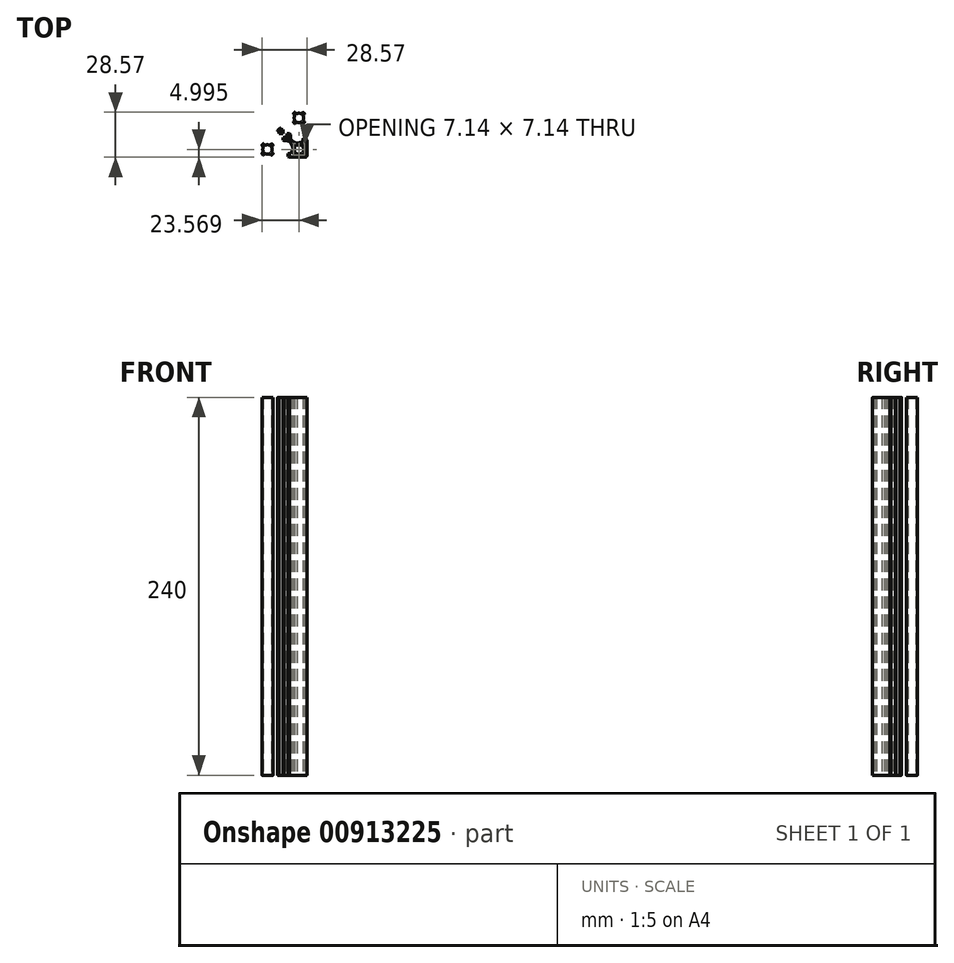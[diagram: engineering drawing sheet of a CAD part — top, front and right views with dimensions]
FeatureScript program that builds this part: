
annotation { "Feature Type Name" : "Feature", "Feature Type Description" : "" }
export const myFeature = defineFeature(function(context is Context, id is Id, definition is map)
    precondition{}
    {
        {
            var Q0;
            Q0=qCreatedBy(makeId("Top.planeOp"),FACE);
            var sketch = newSketch(context, id + "F0", { "sketchPlane" : qUnion([Q0])});
            skLineSegment(sketch, "E0", {"start": v(-71.63, -514.45) * mm, "end": v(-71.63, -402.69) * mm});
            skLineSegment(sketch, "E1", {"start": v(-127.51, -458.57) * mm, "end": v(-15.75, -458.57) * mm});
            skArc(sketch, "E2", {"start": v(-139.86, -492.5) * mm, "mid": v(-139.16, -497.13) * mm, "end": v(-141.3, -501.29) * mm});
            skLineSegment(sketch, "E3", {"start": v(-141.3, -501.29) * mm, "end": v(-160.1, -520.1) * mm});
            skArc(sketch, "E4", {"start": v(-160.1, -520.1) * mm, "mid": v(-162.32, -525.08) * mm, "end": v(-160.65, -530.26) * mm});
            skArc(sketch, "E5", {"start": v(-160.65, -530.26) * mm, "mid": v(-152.46, -539.39) * mm, "end": v(-143.33, -547.58) * mm});
            skArc(sketch, "E6", {"start": v(-143.33, -547.58) * mm, "mid": v(-138.14, -549.26) * mm, "end": v(-133.16, -547.04) * mm});
            skLineSegment(sketch, "E7", {"start": v(-133.16, -547.04) * mm, "end": v(-114.35, -528.23) * mm});
            skArc(sketch, "E8", {"start": v(-114.35, -528.23) * mm, "mid": v(-110.2, -526.1) * mm, "end": v(-105.57, -526.8) * mm});
            skArc(sketch, "E9", {"start": v(-105.57, -526.8) * mm, "mid": v(-71.63, -534.77) * mm, "end": v(-37.7, -526.8) * mm});
            skArc(sketch, "E10", {"start": v(-37.7, -526.8) * mm, "mid": v(-33.07, -526.1) * mm, "end": v(-28.91, -528.23) * mm});
            skLineSegment(sketch, "E11", {"start": v(-28.91, -528.23) * mm, "end": v(-10.1, -547.04) * mm});
            skArc(sketch, "E12", {"start": v(-10.1, -547.04) * mm, "mid": v(-5.12, -549.26) * mm, "end": v(0.06, -547.58) * mm});
            skArc(sketch, "E13", {"start": v(0.06, -547.58) * mm, "mid": v(9.19, -539.39) * mm, "end": v(17.38, -530.26) * mm});
            skArc(sketch, "E14", {"start": v(17.38, -530.26) * mm, "mid": v(19.06, -525.08) * mm, "end": v(16.84, -520.1) * mm});
            skLineSegment(sketch, "E15", {"start": v(16.84, -520.1) * mm, "end": v(-1.97, -501.29) * mm});
            skArc(sketch, "E16", {"start": v(-1.97, -501.29) * mm, "mid": v(-4.1, -497.13) * mm, "end": v(-3.4, -492.5) * mm});
            skArc(sketch, "E17", {"start": v(-3.4, -492.5) * mm, "mid": v(4.57, -458.57) * mm, "end": v(-3.4, -424.63) * mm});
            skArc(sketch, "E18", {"start": v(-3.4, -424.63) * mm, "mid": v(-4.1, -420) * mm, "end": v(-1.97, -415.85) * mm});
            skLineSegment(sketch, "E19", {"start": v(-1.97, -415.85) * mm, "end": v(16.84, -397.04) * mm});
            skArc(sketch, "E20", {"start": v(16.84, -397.04) * mm, "mid": v(19.06, -392.06) * mm, "end": v(17.38, -386.87) * mm});
            skArc(sketch, "E21", {"start": v(17.38, -386.87) * mm, "mid": v(9.19, -377.74) * mm, "end": v(0.06, -369.55) * mm});
            skArc(sketch, "E22", {"start": v(0.06, -369.55) * mm, "mid": v(-5.12, -367.88) * mm, "end": v(-10.1, -370.1) * mm});
            skLineSegment(sketch, "E23", {"start": v(-10.1, -370.1) * mm, "end": v(-28.91, -388.9) * mm});
            skArc(sketch, "E24", {"start": v(-28.91, -388.9) * mm, "mid": v(-33.07, -391.04) * mm, "end": v(-37.7, -390.34) * mm});
            skArc(sketch, "E25", {"start": v(-37.7, -390.34) * mm, "mid": v(-71.63, -382.37) * mm, "end": v(-105.57, -390.34) * mm});
            skArc(sketch, "E26", {"start": v(-105.57, -390.34) * mm, "mid": v(-110.2, -391.04) * mm, "end": v(-114.35, -388.9) * mm});
            skLineSegment(sketch, "E27", {"start": v(-114.35, -388.9) * mm, "end": v(-133.16, -370.1) * mm});
            skArc(sketch, "E28", {"start": v(-133.16, -370.1) * mm, "mid": v(-138.14, -367.88) * mm, "end": v(-143.33, -369.55) * mm});
            skArc(sketch, "E29", {"start": v(-143.33, -369.55) * mm, "mid": v(-152.46, -377.74) * mm, "end": v(-160.65, -386.87) * mm});
            skArc(sketch, "E30", {"start": v(-160.65, -386.87) * mm, "mid": v(-162.32, -392.06) * mm, "end": v(-160.1, -397.04) * mm});
            skLineSegment(sketch, "E31", {"start": v(-160.1, -397.04) * mm, "end": v(-141.3, -415.85) * mm});
            skArc(sketch, "E32", {"start": v(-141.3, -415.85) * mm, "mid": v(-139.16, -420) * mm, "end": v(-139.86, -424.63) * mm});
            skArc(sketch, "E33", {"start": v(-139.86, -424.63) * mm, "mid": v(-147.83, -458.57) * mm, "end": v(-139.86, -492.5) * mm});
            skLineSegment(sketch, "E34", {"start": v(-127.53, -966.58) * mm, "end": v(-15.77, -966.6) * mm});
            skLineSegment(sketch, "E35", {"start": v(-71.65, -910.7) * mm, "end": v(-71.66, -1022.47) * mm});
            skArc(sketch, "E36", {"start": v(-139.88, -932.64) * mm, "mid": v(-139.18, -928.02) * mm, "end": v(-141.3, -923.86) * mm});
            skLineSegment(sketch, "E37", {"start": v(-141.3, -923.86) * mm, "end": v(-160.12, -905.05) * mm});
            skArc(sketch, "E38", {"start": v(-160.12, -905.05) * mm, "mid": v(-162.34, -900.07) * mm, "end": v(-160.66, -894.88) * mm});
            skArc(sketch, "E39", {"start": v(-160.66, -894.88) * mm, "mid": v(-152.47, -885.76) * mm, "end": v(-143.34, -877.56) * mm});
            skArc(sketch, "E40", {"start": v(-143.34, -877.56) * mm, "mid": v(-138.16, -875.9) * mm, "end": v(-133.18, -878.11) * mm});
            skLineSegment(sketch, "E41", {"start": v(-133.18, -878.11) * mm, "end": v(-114.37, -896.92) * mm});
            skArc(sketch, "E42", {"start": v(-114.37, -896.92) * mm, "mid": v(-110.2, -899.06) * mm, "end": v(-105.59, -898.36) * mm});
            skArc(sketch, "E43", {"start": v(-105.59, -898.36) * mm, "mid": v(-71.65, -890.39) * mm, "end": v(-37.71, -898.36) * mm});
            skArc(sketch, "E44", {"start": v(-37.71, -898.36) * mm, "mid": v(-33.09, -899.06) * mm, "end": v(-28.93, -896.93) * mm});
            skLineSegment(sketch, "E45", {"start": v(-28.93, -896.93) * mm, "end": v(-10.12, -878.12) * mm});
            skArc(sketch, "E46", {"start": v(-10.12, -878.12) * mm, "mid": v(-5.14, -875.9) * mm, "end": v(0.05, -877.58) * mm});
            skArc(sketch, "E47", {"start": v(0.05, -877.58) * mm, "mid": v(9.18, -885.77) * mm, "end": v(17.37, -894.9) * mm});
            skArc(sketch, "E48", {"start": v(17.37, -894.9) * mm, "mid": v(19.04, -900.08) * mm, "end": v(16.82, -905.06) * mm});
            skLineSegment(sketch, "E49", {"start": v(16.82, -905.06) * mm, "end": v(-2, -923.87) * mm});
            skArc(sketch, "E50", {"start": v(-2, -923.87) * mm, "mid": v(-4.12, -928.03) * mm, "end": v(-3.43, -932.65) * mm});
            skArc(sketch, "E51", {"start": v(-3.43, -932.65) * mm, "mid": v(4.55, -966.6) * mm, "end": v(-3.43, -1000.53) * mm});
            skArc(sketch, "E52", {"start": v(-3.43, -1000.53) * mm, "mid": v(-4.13, -1005.15) * mm, "end": v(-2, -1009.31) * mm});
            skLineSegment(sketch, "E53", {"start": v(-2, -1009.31) * mm, "end": v(16.81, -1028.12) * mm});
            skArc(sketch, "E54", {"start": v(16.81, -1028.12) * mm, "mid": v(19.03, -1033.1) * mm, "end": v(17.36, -1038.3) * mm});
            skArc(sketch, "E55", {"start": v(17.36, -1038.3) * mm, "mid": v(9.16, -1047.42) * mm, "end": v(0.04, -1055.6) * mm});
            skArc(sketch, "E56", {"start": v(0.04, -1055.6) * mm, "mid": v(-5.15, -1057.28) * mm, "end": v(-10.13, -1055.06) * mm});
            skLineSegment(sketch, "E57", {"start": v(-10.13, -1055.06) * mm, "end": v(-28.94, -1036.25) * mm});
            skArc(sketch, "E58", {"start": v(-28.94, -1036.25) * mm, "mid": v(-33.1, -1034.12) * mm, "end": v(-37.72, -1034.81) * mm});
            skArc(sketch, "E59", {"start": v(-37.72, -1034.81) * mm, "mid": v(-71.66, -1042.79) * mm, "end": v(-105.6, -1034.8) * mm});
            skArc(sketch, "E60", {"start": v(-105.6, -1034.8) * mm, "mid": v(-110.22, -1034.11) * mm, "end": v(-114.38, -1036.24) * mm});
            skLineSegment(sketch, "E61", {"start": v(-114.38, -1036.24) * mm, "end": v(-133.19, -1055.05) * mm});
            skArc(sketch, "E62", {"start": v(-133.19, -1055.05) * mm, "mid": v(-138.17, -1057.27) * mm, "end": v(-143.36, -1055.6) * mm});
            skArc(sketch, "E63", {"start": v(-143.36, -1055.6) * mm, "mid": v(-152.48, -1047.4) * mm, "end": v(-160.68, -1038.28) * mm});
            skArc(sketch, "E64", {"start": v(-160.68, -1038.28) * mm, "mid": v(-162.35, -1033.09) * mm, "end": v(-160.13, -1028.1) * mm});
            skLineSegment(sketch, "E65", {"start": v(-160.13, -1028.1) * mm, "end": v(-141.32, -1009.3) * mm});
            skArc(sketch, "E66", {"start": v(-141.32, -1009.3) * mm, "mid": v(-139.18, -1005.14) * mm, "end": v(-139.88, -1000.52) * mm});
            skArc(sketch, "E67", {"start": v(-139.88, -1000.52) * mm, "mid": v(-147.85, -966.58) * mm, "end": v(-139.88, -932.64) * mm});
            skArc(sketch, "E68", {"start": v(-511.33, -932.64) * mm, "mid": v(-512.03, -928.02) * mm, "end": v(-509.9, -923.86) * mm});
            skLineSegment(sketch, "E69", {"start": v(-509.9, -923.86) * mm, "end": v(-491.09, -905.05) * mm});
            skArc(sketch, "E70", {"start": v(-491.09, -905.05) * mm, "mid": v(-488.87, -900.07) * mm, "end": v(-490.54, -894.88) * mm});
            skArc(sketch, "E71", {"start": v(-490.54, -894.88) * mm, "mid": v(-498.74, -885.76) * mm, "end": v(-507.86, -877.56) * mm});
            skArc(sketch, "E72", {"start": v(-507.86, -877.56) * mm, "mid": v(-513.05, -875.9) * mm, "end": v(-518.03, -878.11) * mm});
            skLineSegment(sketch, "E73", {"start": v(-518.03, -878.11) * mm, "end": v(-536.84, -896.92) * mm});
            skArc(sketch, "E74", {"start": v(-536.84, -896.92) * mm, "mid": v(-541, -899.06) * mm, "end": v(-545.62, -898.36) * mm});
            skArc(sketch, "E75", {"start": v(-545.62, -898.36) * mm, "mid": v(-579.56, -890.39) * mm, "end": v(-613.5, -898.36) * mm});
            skArc(sketch, "E76", {"start": v(-613.5, -898.36) * mm, "mid": v(-618.12, -899.06) * mm, "end": v(-622.28, -896.93) * mm});
            skLineSegment(sketch, "E77", {"start": v(-622.28, -896.93) * mm, "end": v(-641.1, -878.12) * mm});
            skArc(sketch, "E78", {"start": v(-641.1, -878.12) * mm, "mid": v(-646.07, -875.9) * mm, "end": v(-651.26, -877.58) * mm});
            skArc(sketch, "E79", {"start": v(-651.26, -877.58) * mm, "mid": v(-660.38, -885.77) * mm, "end": v(-668.58, -894.9) * mm});
            skArc(sketch, "E80", {"start": v(-668.58, -894.9) * mm, "mid": v(-670.25, -900.08) * mm, "end": v(-668.03, -905.06) * mm});
            skLineSegment(sketch, "E81", {"start": v(-668.03, -905.06) * mm, "end": v(-649.22, -923.87) * mm});
            skArc(sketch, "E82", {"start": v(-649.22, -923.87) * mm, "mid": v(-647.08, -928.03) * mm, "end": v(-647.78, -932.65) * mm});
            skArc(sketch, "E83", {"start": v(-647.78, -932.65) * mm, "mid": v(-655.75, -966.6) * mm, "end": v(-647.78, -1000.53) * mm});
            skArc(sketch, "E84", {"start": v(-647.78, -1000.53) * mm, "mid": v(-647.08, -1005.15) * mm, "end": v(-649.21, -1009.31) * mm});
            skLineSegment(sketch, "E85", {"start": v(-649.21, -1009.31) * mm, "end": v(-668.02, -1028.12) * mm});
            skArc(sketch, "E86", {"start": v(-668.02, -1028.12) * mm, "mid": v(-670.24, -1033.1) * mm, "end": v(-668.57, -1038.3) * mm});
            skArc(sketch, "E87", {"start": v(-668.57, -1038.3) * mm, "mid": v(-660.37, -1047.42) * mm, "end": v(-651.24, -1055.6) * mm});
            skArc(sketch, "E88", {"start": v(-651.24, -1055.6) * mm, "mid": v(-646.06, -1057.28) * mm, "end": v(-641.08, -1055.06) * mm});
            skLineSegment(sketch, "E89", {"start": v(-641.08, -1055.06) * mm, "end": v(-622.27, -1036.25) * mm});
            skArc(sketch, "E90", {"start": v(-622.27, -1036.25) * mm, "mid": v(-618.1, -1034.12) * mm, "end": v(-613.49, -1034.81) * mm});
            skArc(sketch, "E91", {"start": v(-613.49, -1034.81) * mm, "mid": v(-579.55, -1042.79) * mm, "end": v(-545.61, -1034.8) * mm});
            skArc(sketch, "E92", {"start": v(-545.61, -1034.8) * mm, "mid": v(-540.99, -1034.11) * mm, "end": v(-536.83, -1036.24) * mm});
            skLineSegment(sketch, "E93", {"start": v(-536.83, -1036.24) * mm, "end": v(-518.02, -1055.05) * mm});
            skArc(sketch, "E94", {"start": v(-518.02, -1055.05) * mm, "mid": v(-513.04, -1057.27) * mm, "end": v(-507.85, -1055.6) * mm});
            skArc(sketch, "E95", {"start": v(-507.85, -1055.6) * mm, "mid": v(-498.73, -1047.4) * mm, "end": v(-490.53, -1038.28) * mm});
            skArc(sketch, "E96", {"start": v(-490.53, -1038.28) * mm, "mid": v(-488.86, -1033.09) * mm, "end": v(-491.08, -1028.1) * mm});
            skLineSegment(sketch, "E97", {"start": v(-491.08, -1028.1) * mm, "end": v(-509.9, -1009.3) * mm});
            skArc(sketch, "E98", {"start": v(-509.9, -1009.3) * mm, "mid": v(-512.02, -1005.14) * mm, "end": v(-511.33, -1000.52) * mm});
            skArc(sketch, "E99", {"start": v(-511.33, -1000.52) * mm, "mid": v(-503.35, -966.58) * mm, "end": v(-511.33, -932.64) * mm});
            skLineSegment(sketch, "E100", {"start": v(-579.56, -910.7) * mm, "end": v(-579.55, -1022.47) * mm});
            skLineSegment(sketch, "E101", {"start": v(-523.67, -966.58) * mm, "end": v(-635.43, -966.6) * mm});
            skLineSegment(sketch, "E102", {"start": v(-523.7, -458.57) * mm, "end": v(-635.45, -458.57) * mm});
            skLineSegment(sketch, "E103", {"start": v(-579.57, -514.45) * mm, "end": v(-579.57, -402.69) * mm});
            skLineSegment(sketch, "E104", {"start": v(67.05, -712.57) * mm, "end": v(-737.67, -712.57) * mm});
            skLineSegment(sketch, "E105", {"start": v(-325.57, -1117.47) * mm, "end": v(-325.57, -306.26) * mm});
            skArc(sketch, "E106", {"start": v(-243.35, -672.28) * mm, "mid": v(-237.77, -667.95) * mm, "end": v(-238.14, -660.9) * mm});
            skArc(sketch, "E107", {"start": v(-238.14, -660.9) * mm, "mid": v(-253.76, -640.75) * mm, "end": v(-273.91, -625.13) * mm});
            skArc(sketch, "E108", {"start": v(-273.91, -625.13) * mm, "mid": v(-280.96, -624.76) * mm, "end": v(-285.29, -630.34) * mm});
            skLineSegment(sketch, "E109", {"start": v(-285.29, -630.34) * mm, "end": v(-288.68, -649.16) * mm});
            skArc(sketch, "E110", {"start": v(-288.68, -649.16) * mm, "mid": v(-292.64, -654.55) * mm, "end": v(-299.33, -654.74) * mm});
            skArc(sketch, "E111", {"start": v(-299.33, -654.74) * mm, "mid": v(-325.57, -649.07) * mm, "end": v(-351.82, -654.74) * mm});
            skArc(sketch, "E112", {"start": v(-351.82, -654.74) * mm, "mid": v(-358.51, -654.55) * mm, "end": v(-362.47, -649.16) * mm});
            skLineSegment(sketch, "E113", {"start": v(-362.47, -649.16) * mm, "end": v(-365.86, -630.34) * mm});
            skArc(sketch, "E114", {"start": v(-365.86, -630.34) * mm, "mid": v(-370.19, -624.76) * mm, "end": v(-377.24, -625.13) * mm});
            skArc(sketch, "E115", {"start": v(-377.24, -625.13) * mm, "mid": v(-397.39, -640.75) * mm, "end": v(-413.01, -660.9) * mm});
            skArc(sketch, "E116", {"start": v(-413.01, -660.9) * mm, "mid": v(-413.38, -667.95) * mm, "end": v(-407.8, -672.28) * mm});
            skLineSegment(sketch, "E117", {"start": v(-407.8, -672.28) * mm, "end": v(-388.98, -675.67) * mm});
            skArc(sketch, "E118", {"start": v(-388.98, -675.67) * mm, "mid": v(-383.59, -679.63) * mm, "end": v(-383.4, -686.32) * mm});
            skArc(sketch, "E119", {"start": v(-383.4, -686.32) * mm, "mid": v(-389.07, -712.57) * mm, "end": v(-383.4, -738.81) * mm});
            skArc(sketch, "E120", {"start": v(-383.4, -738.81) * mm, "mid": v(-383.59, -745.5) * mm, "end": v(-388.98, -749.46) * mm});
            skLineSegment(sketch, "E121", {"start": v(-388.98, -749.46) * mm, "end": v(-407.8, -752.85) * mm});
            skArc(sketch, "E122", {"start": v(-407.8, -752.85) * mm, "mid": v(-413.38, -757.18) * mm, "end": v(-413.01, -764.23) * mm});
            skArc(sketch, "E123", {"start": v(-413.01, -764.23) * mm, "mid": v(-397.39, -784.38) * mm, "end": v(-377.24, -800) * mm});
            skArc(sketch, "E124", {"start": v(-377.24, -800) * mm, "mid": v(-370.19, -800.37) * mm, "end": v(-365.86, -794.8) * mm});
            skLineSegment(sketch, "E125", {"start": v(-365.86, -794.8) * mm, "end": v(-362.47, -775.98) * mm});
            skArc(sketch, "E126", {"start": v(-362.47, -775.98) * mm, "mid": v(-358.51, -770.58) * mm, "end": v(-351.82, -770.39) * mm});
            skArc(sketch, "E127", {"start": v(-351.82, -770.39) * mm, "mid": v(-325.57, -776.07) * mm, "end": v(-299.33, -770.39) * mm});
            skArc(sketch, "E128", {"start": v(-299.33, -770.39) * mm, "mid": v(-292.64, -770.58) * mm, "end": v(-288.68, -775.98) * mm});
            skLineSegment(sketch, "E129", {"start": v(-288.68, -775.98) * mm, "end": v(-285.29, -794.8) * mm});
            skArc(sketch, "E130", {"start": v(-285.29, -794.8) * mm, "mid": v(-280.96, -800.37) * mm, "end": v(-273.91, -800) * mm});
            skArc(sketch, "E131", {"start": v(-273.91, -800) * mm, "mid": v(-253.76, -784.38) * mm, "end": v(-238.14, -764.23) * mm});
            skArc(sketch, "E132", {"start": v(-238.14, -764.23) * mm, "mid": v(-237.77, -757.18) * mm, "end": v(-243.35, -752.85) * mm});
            skLineSegment(sketch, "E133", {"start": v(-243.35, -752.85) * mm, "end": v(-262.17, -749.46) * mm});
            skArc(sketch, "E134", {"start": v(-262.17, -749.46) * mm, "mid": v(-267.56, -745.5) * mm, "end": v(-267.75, -738.81) * mm});
            skArc(sketch, "E135", {"start": v(-267.75, -738.81) * mm, "mid": v(-262.07, -712.57) * mm, "end": v(-267.75, -686.32) * mm});
            skArc(sketch, "E136", {"start": v(-267.75, -686.32) * mm, "mid": v(-267.56, -679.63) * mm, "end": v(-262.17, -675.67) * mm});
            skLineSegment(sketch, "E137", {"start": v(-262.17, -675.67) * mm, "end": v(-243.35, -672.28) * mm});
            skArc(sketch, "E138", {"start": v(-511.35, -492.5) * mm, "mid": v(-512.05, -497.13) * mm, "end": v(-509.91, -501.29) * mm});
            skLineSegment(sketch, "E139", {"start": v(-509.91, -501.29) * mm, "end": v(-491.1, -520.1) * mm});
            skArc(sketch, "E140", {"start": v(-491.1, -520.1) * mm, "mid": v(-488.88, -525.08) * mm, "end": v(-490.56, -530.26) * mm});
            skArc(sketch, "E141", {"start": v(-490.56, -530.26) * mm, "mid": v(-498.75, -539.39) * mm, "end": v(-507.88, -547.58) * mm});
            skArc(sketch, "E142", {"start": v(-507.88, -547.58) * mm, "mid": v(-513.07, -549.26) * mm, "end": v(-518.04, -547.04) * mm});
            skLineSegment(sketch, "E143", {"start": v(-518.04, -547.04) * mm, "end": v(-536.86, -528.23) * mm});
            skArc(sketch, "E144", {"start": v(-536.86, -528.23) * mm, "mid": v(-541.01, -526.1) * mm, "end": v(-545.64, -526.8) * mm});
            skArc(sketch, "E145", {"start": v(-545.64, -526.8) * mm, "mid": v(-579.57, -534.77) * mm, "end": v(-613.51, -526.8) * mm});
            skArc(sketch, "E146", {"start": v(-613.51, -526.8) * mm, "mid": v(-618.13, -526.1) * mm, "end": v(-622.3, -528.23) * mm});
            skLineSegment(sketch, "E147", {"start": v(-622.3, -528.23) * mm, "end": v(-641.1, -547.04) * mm});
            skArc(sketch, "E148", {"start": v(-641.1, -547.04) * mm, "mid": v(-646.08, -549.26) * mm, "end": v(-651.27, -547.58) * mm});
            skArc(sketch, "E149", {"start": v(-651.27, -547.58) * mm, "mid": v(-660.4, -539.39) * mm, "end": v(-668.6, -530.26) * mm});
            skArc(sketch, "E150", {"start": v(-668.6, -530.26) * mm, "mid": v(-670.27, -525.08) * mm, "end": v(-668.04, -520.1) * mm});
            skLineSegment(sketch, "E151", {"start": v(-668.04, -520.1) * mm, "end": v(-649.23, -501.29) * mm});
            skArc(sketch, "E152", {"start": v(-649.23, -501.29) * mm, "mid": v(-647.1, -497.13) * mm, "end": v(-647.8, -492.5) * mm});
            skArc(sketch, "E153", {"start": v(-647.8, -492.5) * mm, "mid": v(-655.77, -458.57) * mm, "end": v(-647.8, -424.63) * mm});
            skArc(sketch, "E154", {"start": v(-647.8, -424.63) * mm, "mid": v(-647.1, -420) * mm, "end": v(-649.23, -415.85) * mm});
            skLineSegment(sketch, "E155", {"start": v(-649.23, -415.85) * mm, "end": v(-668.04, -397.04) * mm});
            skArc(sketch, "E156", {"start": v(-668.04, -397.04) * mm, "mid": v(-670.27, -392.06) * mm, "end": v(-668.6, -386.87) * mm});
            skArc(sketch, "E157", {"start": v(-668.6, -386.87) * mm, "mid": v(-660.4, -377.74) * mm, "end": v(-651.27, -369.55) * mm});
            skArc(sketch, "E158", {"start": v(-651.27, -369.55) * mm, "mid": v(-646.08, -367.88) * mm, "end": v(-641.1, -370.1) * mm});
            skLineSegment(sketch, "E159", {"start": v(-641.1, -370.1) * mm, "end": v(-622.3, -388.9) * mm});
            skArc(sketch, "E160", {"start": v(-622.3, -388.9) * mm, "mid": v(-618.13, -391.04) * mm, "end": v(-613.51, -390.34) * mm});
            skArc(sketch, "E161", {"start": v(-613.51, -390.34) * mm, "mid": v(-579.57, -382.37) * mm, "end": v(-545.64, -390.34) * mm});
            skArc(sketch, "E162", {"start": v(-545.64, -390.34) * mm, "mid": v(-541.01, -391.04) * mm, "end": v(-536.86, -388.9) * mm});
            skLineSegment(sketch, "E163", {"start": v(-536.86, -388.9) * mm, "end": v(-518.04, -370.1) * mm});
            skArc(sketch, "E164", {"start": v(-518.04, -370.1) * mm, "mid": v(-513.07, -367.88) * mm, "end": v(-507.88, -369.55) * mm});
            skArc(sketch, "E165", {"start": v(-507.88, -369.55) * mm, "mid": v(-498.75, -377.74) * mm, "end": v(-490.56, -386.87) * mm});
            skArc(sketch, "E166", {"start": v(-490.56, -386.87) * mm, "mid": v(-488.88, -392.06) * mm, "end": v(-491.1, -397.04) * mm});
            skLineSegment(sketch, "E167", {"start": v(-491.1, -397.04) * mm, "end": v(-509.91, -415.85) * mm});
            skArc(sketch, "E168", {"start": v(-509.91, -415.85) * mm, "mid": v(-512.05, -420) * mm, "end": v(-511.35, -424.63) * mm});
            skArc(sketch, "E169", {"start": v(-511.35, -424.63) * mm, "mid": v(-503.37, -458.57) * mm, "end": v(-511.35, -492.5) * mm});
            skLineSegment(sketch, "E170", {"start": v(-225.24, -1093.57) * mm, "end": v(-245.56, -1080.87) * mm});
            skLineSegment(sketch, "E171", {"start": v(-245.56, -1080.87) * mm, "end": v(-245.56, -1037.69) * mm});
            skArc(sketch, "E172", {"start": v(-245.56, -1037.69) * mm, "mid": v(-243.33, -1032.3) * mm, "end": v(-237.94, -1030.07) * mm});
            skLineSegment(sketch, "E173", {"start": v(-237.94, -1030.07) * mm, "end": v(-196.03, -1030.07) * mm});
            skLineSegment(sketch, "E174", {"start": v(-196.03, -1030.07) * mm, "end": v(-170.95, -952.55) * mm});
            skArc(sketch, "E175", {"start": v(-170.95, -952.55) * mm, "mid": v(-169.75, -945.99) * mm, "end": v(-170.3, -939.33) * mm});
            skArc(sketch, "E176", {"start": v(-170.3, -939.33) * mm, "mid": v(-191.6, -887.57) * mm, "end": v(-223.87, -841.84) * mm});
            skArc(sketch, "E177", {"start": v(-223.87, -841.84) * mm, "mid": v(-245.35, -830.7) * mm, "end": v(-269.24, -826.87) * mm});
            skLineSegment(sketch, "E178", {"start": v(-269.24, -826.87) * mm, "end": v(-312.87, -826.87) * mm});
            skLineSegment(sketch, "E179", {"start": v(-312.87, -826.87) * mm, "end": v(-325.57, -814.17) * mm});
            skLineSegment(sketch, "E180", {"start": v(-325.57, -814.17) * mm, "end": v(-338.27, -826.87) * mm});
            skLineSegment(sketch, "E181", {"start": v(-338.27, -826.87) * mm, "end": v(-381.9, -826.87) * mm});
            skArc(sketch, "E182", {"start": v(-381.9, -826.87) * mm, "mid": v(-405.8, -830.7) * mm, "end": v(-427.28, -841.84) * mm});
            skArc(sketch, "E183", {"start": v(-427.28, -841.84) * mm, "mid": v(-459.55, -887.57) * mm, "end": v(-480.85, -939.33) * mm});
            skArc(sketch, "E184", {"start": v(-480.85, -939.33) * mm, "mid": v(-481.4, -945.99) * mm, "end": v(-480.2, -952.55) * mm});
            skLineSegment(sketch, "E185", {"start": v(-480.2, -952.55) * mm, "end": v(-455.11, -1030.07) * mm});
            skLineSegment(sketch, "E186", {"start": v(-455.11, -1030.07) * mm, "end": v(-413.2, -1030.07) * mm});
            skArc(sketch, "E187", {"start": v(-413.2, -1030.07) * mm, "mid": v(-407.82, -1032.3) * mm, "end": v(-405.58, -1037.69) * mm});
            skLineSegment(sketch, "E188", {"start": v(-405.58, -1037.69) * mm, "end": v(-405.58, -1080.87) * mm});
            skLineSegment(sketch, "E189", {"start": v(-405.58, -1080.87) * mm, "end": v(-425.9, -1093.57) * mm});
            skLineSegment(sketch, "E190", {"start": v(-425.9, -1093.57) * mm, "end": v(-681.17, -1093.57) * mm});
            skArc(sketch, "E191", {"start": v(-681.17, -1093.57) * mm, "mid": v(-699.13, -1086.13) * mm, "end": v(-706.57, -1068.17) * mm});
            skLineSegment(sketch, "E192", {"start": v(-706.57, -1068.17) * mm, "end": v(-706.57, -812.9) * mm});
            skLineSegment(sketch, "E193", {"start": v(-706.57, -812.9) * mm, "end": v(-693.87, -792.58) * mm});
            skLineSegment(sketch, "E194", {"start": v(-693.87, -792.58) * mm, "end": v(-650.7, -792.58) * mm});
            skArc(sketch, "E195", {"start": v(-650.7, -792.58) * mm, "mid": v(-645.3, -794.8) * mm, "end": v(-643.07, -800.2) * mm});
            skLineSegment(sketch, "E196", {"start": v(-643.07, -800.2) * mm, "end": v(-643.07, -842.1) * mm});
            skLineSegment(sketch, "E197", {"start": v(-643.07, -842.1) * mm, "end": v(-565.56, -867.2) * mm});
            skArc(sketch, "E198", {"start": v(-565.56, -867.2) * mm, "mid": v(-559, -868.4) * mm, "end": v(-552.34, -867.85) * mm});
            skArc(sketch, "E199", {"start": v(-552.34, -867.85) * mm, "mid": v(-500.58, -846.54) * mm, "end": v(-454.85, -814.27) * mm});
            skArc(sketch, "E200", {"start": v(-454.85, -814.27) * mm, "mid": v(-443.72, -792.79) * mm, "end": v(-439.87, -768.9) * mm});
            skLineSegment(sketch, "E201", {"start": v(-439.87, -768.9) * mm, "end": v(-439.87, -725.27) * mm});
            skLineSegment(sketch, "E202", {"start": v(-439.87, -725.27) * mm, "end": v(-427.17, -712.57) * mm});
            skLineSegment(sketch, "E203", {"start": v(-427.17, -712.57) * mm, "end": v(-439.87, -699.87) * mm});
            skLineSegment(sketch, "E204", {"start": v(-439.87, -699.87) * mm, "end": v(-439.87, -656.23) * mm});
            skArc(sketch, "E205", {"start": v(-439.87, -656.23) * mm, "mid": v(-443.72, -632.34) * mm, "end": v(-454.85, -610.86) * mm});
            skArc(sketch, "E206", {"start": v(-454.85, -610.86) * mm, "mid": v(-500.58, -578.6) * mm, "end": v(-552.34, -557.29) * mm});
            skArc(sketch, "E207", {"start": v(-552.34, -557.29) * mm, "mid": v(-559, -556.74) * mm, "end": v(-565.56, -557.94) * mm});
            skLineSegment(sketch, "E208", {"start": v(-565.56, -557.94) * mm, "end": v(-643.07, -583.03) * mm});
            skLineSegment(sketch, "E209", {"start": v(-643.07, -583.03) * mm, "end": v(-643.07, -624.94) * mm});
            skArc(sketch, "E210", {"start": v(-643.07, -624.94) * mm, "mid": v(-645.3, -630.32) * mm, "end": v(-650.7, -632.56) * mm});
            skLineSegment(sketch, "E211", {"start": v(-650.7, -632.56) * mm, "end": v(-693.87, -632.56) * mm});
            skLineSegment(sketch, "E212", {"start": v(-693.87, -632.56) * mm, "end": v(-706.57, -612.24) * mm});
            skLineSegment(sketch, "E213", {"start": v(-706.57, -612.24) * mm, "end": v(-706.57, -356.97) * mm});
            skArc(sketch, "E214", {"start": v(-706.57, -356.97) * mm, "mid": v(-699.13, -339) * mm, "end": v(-681.17, -331.57) * mm});
            skLineSegment(sketch, "E215", {"start": v(-681.17, -331.57) * mm, "end": v(-425.9, -331.57) * mm});
            skLineSegment(sketch, "E216", {"start": v(-425.9, -331.57) * mm, "end": v(-405.58, -344.27) * mm});
            skLineSegment(sketch, "E217", {"start": v(-405.58, -344.27) * mm, "end": v(-405.58, -387.45) * mm});
            skArc(sketch, "E218", {"start": v(-405.58, -387.45) * mm, "mid": v(-407.82, -392.83) * mm, "end": v(-413.2, -395.07) * mm});
            skLineSegment(sketch, "E219", {"start": v(-413.2, -395.07) * mm, "end": v(-455.11, -395.07) * mm});
            skLineSegment(sketch, "E220", {"start": v(-455.11, -395.07) * mm, "end": v(-480.2, -472.58) * mm});
            skArc(sketch, "E221", {"start": v(-480.2, -472.58) * mm, "mid": v(-481.4, -479.15) * mm, "end": v(-480.85, -485.8) * mm});
            skArc(sketch, "E222", {"start": v(-480.85, -485.8) * mm, "mid": v(-459.55, -537.56) * mm, "end": v(-427.28, -583.29) * mm});
            skArc(sketch, "E223", {"start": v(-427.28, -583.29) * mm, "mid": v(-405.8, -594.43) * mm, "end": v(-381.9, -598.27) * mm});
            skLineSegment(sketch, "E224", {"start": v(-381.9, -598.27) * mm, "end": v(-338.27, -598.27) * mm});
            skLineSegment(sketch, "E225", {"start": v(-338.27, -598.27) * mm, "end": v(-325.57, -610.97) * mm});
            skLineSegment(sketch, "E226", {"start": v(-325.57, -610.97) * mm, "end": v(-312.87, -598.27) * mm});
            skLineSegment(sketch, "E227", {"start": v(-312.87, -598.27) * mm, "end": v(-269.24, -598.27) * mm});
            skArc(sketch, "E228", {"start": v(-269.24, -598.27) * mm, "mid": v(-245.35, -594.43) * mm, "end": v(-223.87, -583.29) * mm});
            skArc(sketch, "E229", {"start": v(-223.87, -583.29) * mm, "mid": v(-191.6, -537.56) * mm, "end": v(-170.3, -485.8) * mm});
            skArc(sketch, "E230", {"start": v(-170.3, -485.8) * mm, "mid": v(-169.75, -479.15) * mm, "end": v(-170.95, -472.58) * mm});
            skLineSegment(sketch, "E231", {"start": v(-170.95, -472.58) * mm, "end": v(-196.03, -395.07) * mm});
            skLineSegment(sketch, "E232", {"start": v(-196.03, -395.07) * mm, "end": v(-237.94, -395.07) * mm});
            skArc(sketch, "E233", {"start": v(-237.94, -395.07) * mm, "mid": v(-243.33, -392.83) * mm, "end": v(-245.56, -387.45) * mm});
            skLineSegment(sketch, "E234", {"start": v(-245.56, -387.45) * mm, "end": v(-245.56, -344.27) * mm});
            skLineSegment(sketch, "E235", {"start": v(-245.56, -344.27) * mm, "end": v(-225.24, -331.57) * mm});
            skLineSegment(sketch, "E236", {"start": v(-225.24, -331.57) * mm, "end": v(30.03, -331.57) * mm});
            skArc(sketch, "E237", {"start": v(30.03, -331.57) * mm, "mid": v(47.99, -339) * mm, "end": v(55.43, -356.97) * mm});
            skLineSegment(sketch, "E238", {"start": v(55.43, -356.97) * mm, "end": v(55.43, -612.24) * mm});
            skLineSegment(sketch, "E239", {"start": v(55.43, -612.24) * mm, "end": v(42.73, -632.56) * mm});
            skLineSegment(sketch, "E240", {"start": v(42.73, -632.56) * mm, "end": v(-0.45, -632.56) * mm});
            skArc(sketch, "E241", {"start": v(-0.45, -632.56) * mm, "mid": v(-5.84, -630.32) * mm, "end": v(-8.07, -624.94) * mm});
            skLineSegment(sketch, "E242", {"start": v(-8.07, -624.94) * mm, "end": v(-8.07, -583.03) * mm});
            skLineSegment(sketch, "E243", {"start": v(-8.07, -583.03) * mm, "end": v(-85.59, -557.94) * mm});
            skArc(sketch, "E244", {"start": v(-85.59, -557.94) * mm, "mid": v(-92.15, -556.74) * mm, "end": v(-98.8, -557.29) * mm});
            skArc(sketch, "E245", {"start": v(-98.8, -557.29) * mm, "mid": v(-150.57, -578.6) * mm, "end": v(-196.3, -610.86) * mm});
            skArc(sketch, "E246", {"start": v(-196.3, -610.86) * mm, "mid": v(-207.43, -632.34) * mm, "end": v(-211.27, -656.23) * mm});
            skLineSegment(sketch, "E247", {"start": v(-211.27, -656.23) * mm, "end": v(-211.27, -699.87) * mm});
            skLineSegment(sketch, "E248", {"start": v(-211.27, -699.87) * mm, "end": v(-223.97, -712.57) * mm});
            skLineSegment(sketch, "E249", {"start": v(-223.97, -712.57) * mm, "end": v(-211.27, -725.27) * mm});
            skLineSegment(sketch, "E250", {"start": v(-211.27, -725.27) * mm, "end": v(-211.27, -768.9) * mm});
            skArc(sketch, "E251", {"start": v(-211.27, -768.9) * mm, "mid": v(-207.43, -792.79) * mm, "end": v(-196.3, -814.27) * mm});
            skArc(sketch, "E252", {"start": v(-196.3, -814.27) * mm, "mid": v(-150.57, -846.54) * mm, "end": v(-98.8, -867.85) * mm});
            skArc(sketch, "E253", {"start": v(-98.8, -867.85) * mm, "mid": v(-92.15, -868.4) * mm, "end": v(-85.59, -867.2) * mm});
            skLineSegment(sketch, "E254", {"start": v(-85.59, -867.2) * mm, "end": v(-8.07, -842.1) * mm});
            skLineSegment(sketch, "E255", {"start": v(-8.07, -842.1) * mm, "end": v(-8.07, -800.2) * mm});
            skArc(sketch, "E256", {"start": v(-8.07, -800.2) * mm, "mid": v(-5.84, -794.8) * mm, "end": v(-0.45, -792.58) * mm});
            skLineSegment(sketch, "E257", {"start": v(-0.45, -792.58) * mm, "end": v(42.73, -792.58) * mm});
            skLineSegment(sketch, "E258", {"start": v(42.73, -792.58) * mm, "end": v(55.43, -812.9) * mm});
            skLineSegment(sketch, "E259", {"start": v(55.43, -812.9) * mm, "end": v(55.43, -1068.17) * mm});
            skArc(sketch, "E260", {"start": v(55.43, -1068.17) * mm, "mid": v(47.99, -1086.13) * mm, "end": v(30.03, -1093.57) * mm});
            skLineSegment(sketch, "E261", {"start": v(30.03, -1093.57) * mm, "end": v(-225.24, -1093.57) * mm});
            skLineSegment(sketch, "E262", {"start": v(465.62, 205.58) * mm, "end": v(465.62, 209.98) * mm});
            skLineSegment(sketch, "E263", {"start": v(463.42, 207.78) * mm, "end": v(467.82, 207.78) * mm});
            skArc(sketch, "E264", {"start": v(462.94, 206.45) * mm, "mid": v(462.96, 206.27) * mm, "end": v(462.88, 206.1) * mm});
            skLineSegment(sketch, "E265", {"start": v(462.88, 206.1) * mm, "end": v(462.14, 205.36) * mm});
            skArc(sketch, "E266", {"start": v(462.14, 205.36) * mm, "mid": v(462.05, 205.17) * mm, "end": v(462.12, 204.96) * mm});
            skArc(sketch, "E267", {"start": v(462.12, 204.96) * mm, "mid": v(462.44, 204.6) * mm, "end": v(462.8, 204.28) * mm});
            skArc(sketch, "E268", {"start": v(462.8, 204.28) * mm, "mid": v(463, 204.21) * mm, "end": v(463.2, 204.3) * mm});
            skLineSegment(sketch, "E269", {"start": v(463.2, 204.3) * mm, "end": v(463.94, 205.04) * mm});
            skArc(sketch, "E270", {"start": v(463.94, 205.04) * mm, "mid": v(464.1, 205.13) * mm, "end": v(464.29, 205.1) * mm});
            skArc(sketch, "E271", {"start": v(464.29, 205.1) * mm, "mid": v(465.62, 204.78) * mm, "end": v(466.96, 205.1) * mm});
            skArc(sketch, "E272", {"start": v(466.96, 205.1) * mm, "mid": v(467.14, 205.13) * mm, "end": v(467.3, 205.04) * mm});
            skLineSegment(sketch, "E273", {"start": v(467.3, 205.04) * mm, "end": v(468.04, 204.3) * mm});
            skArc(sketch, "E274", {"start": v(468.04, 204.3) * mm, "mid": v(468.24, 204.21) * mm, "end": v(468.44, 204.28) * mm});
            skArc(sketch, "E275", {"start": v(468.44, 204.28) * mm, "mid": v(468.8, 204.6) * mm, "end": v(469.13, 204.96) * mm});
            skArc(sketch, "E276", {"start": v(469.13, 204.96) * mm, "mid": v(469.2, 205.17) * mm, "end": v(469.1, 205.36) * mm});
            skLineSegment(sketch, "E277", {"start": v(469.1, 205.36) * mm, "end": v(468.36, 206.1) * mm});
            skArc(sketch, "E278", {"start": v(468.36, 206.1) * mm, "mid": v(468.28, 206.27) * mm, "end": v(468.3, 206.45) * mm});
            skArc(sketch, "E279", {"start": v(468.3, 206.45) * mm, "mid": v(468.62, 207.78) * mm, "end": v(468.3, 209.12) * mm});
            skArc(sketch, "E280", {"start": v(468.3, 209.12) * mm, "mid": v(468.28, 209.3) * mm, "end": v(468.36, 209.47) * mm});
            skLineSegment(sketch, "E281", {"start": v(468.36, 209.47) * mm, "end": v(469.1, 210.2) * mm});
            skArc(sketch, "E282", {"start": v(469.1, 210.2) * mm, "mid": v(469.2, 210.4) * mm, "end": v(469.13, 210.6) * mm});
            skArc(sketch, "E283", {"start": v(469.13, 210.6) * mm, "mid": v(468.8, 210.97) * mm, "end": v(468.44, 211.29) * mm});
            skArc(sketch, "E284", {"start": v(468.44, 211.29) * mm, "mid": v(468.24, 211.35) * mm, "end": v(468.04, 211.27) * mm});
            skLineSegment(sketch, "E285", {"start": v(468.04, 211.27) * mm, "end": v(467.3, 210.53) * mm});
            skArc(sketch, "E286", {"start": v(467.3, 210.53) * mm, "mid": v(467.14, 210.44) * mm, "end": v(466.96, 210.47) * mm});
            skArc(sketch, "E287", {"start": v(466.96, 210.47) * mm, "mid": v(465.62, 210.78) * mm, "end": v(464.29, 210.47) * mm});
            skArc(sketch, "E288", {"start": v(464.29, 210.47) * mm, "mid": v(464.1, 210.44) * mm, "end": v(463.94, 210.53) * mm});
            skLineSegment(sketch, "E289", {"start": v(463.94, 210.53) * mm, "end": v(463.2, 211.27) * mm});
            skArc(sketch, "E290", {"start": v(463.2, 211.27) * mm, "mid": v(463, 211.35) * mm, "end": v(462.8, 211.29) * mm});
            skArc(sketch, "E291", {"start": v(462.8, 211.29) * mm, "mid": v(462.44, 210.97) * mm, "end": v(462.12, 210.6) * mm});
            skArc(sketch, "E292", {"start": v(462.12, 210.6) * mm, "mid": v(462.05, 210.4) * mm, "end": v(462.14, 210.2) * mm});
            skLineSegment(sketch, "E293", {"start": v(462.14, 210.2) * mm, "end": v(462.88, 209.47) * mm});
            skArc(sketch, "E294", {"start": v(462.88, 209.47) * mm, "mid": v(462.96, 209.3) * mm, "end": v(462.94, 209.12) * mm});
            skArc(sketch, "E295", {"start": v(462.94, 209.12) * mm, "mid": v(462.62, 207.78) * mm, "end": v(462.94, 206.45) * mm});
            skLineSegment(sketch, "E296", {"start": v(463.42, 187.78) * mm, "end": v(467.82, 187.78) * mm});
            skLineSegment(sketch, "E297", {"start": v(465.62, 189.98) * mm, "end": v(465.62, 185.58) * mm});
            skArc(sketch, "E298", {"start": v(462.94, 189.12) * mm, "mid": v(462.96, 189.3) * mm, "end": v(462.88, 189.47) * mm});
            skLineSegment(sketch, "E299", {"start": v(462.88, 189.47) * mm, "end": v(462.14, 190.2) * mm});
            skArc(sketch, "E300", {"start": v(462.14, 190.2) * mm, "mid": v(462.05, 190.4) * mm, "end": v(462.12, 190.6) * mm});
            skArc(sketch, "E301", {"start": v(462.12, 190.6) * mm, "mid": v(462.44, 190.97) * mm, "end": v(462.8, 191.29) * mm});
            skArc(sketch, "E302", {"start": v(462.8, 191.29) * mm, "mid": v(463, 191.35) * mm, "end": v(463.2, 191.27) * mm});
            skLineSegment(sketch, "E303", {"start": v(463.2, 191.27) * mm, "end": v(463.94, 190.53) * mm});
            skArc(sketch, "E304", {"start": v(463.94, 190.53) * mm, "mid": v(464.1, 190.44) * mm, "end": v(464.29, 190.47) * mm});
            skArc(sketch, "E305", {"start": v(464.29, 190.47) * mm, "mid": v(465.62, 190.78) * mm, "end": v(466.96, 190.47) * mm});
            skArc(sketch, "E306", {"start": v(466.96, 190.47) * mm, "mid": v(467.14, 190.44) * mm, "end": v(467.3, 190.53) * mm});
            skLineSegment(sketch, "E307", {"start": v(467.3, 190.53) * mm, "end": v(468.04, 191.27) * mm});
            skArc(sketch, "E308", {"start": v(468.04, 191.27) * mm, "mid": v(468.24, 191.35) * mm, "end": v(468.44, 191.29) * mm});
            skArc(sketch, "E309", {"start": v(468.44, 191.29) * mm, "mid": v(468.8, 190.96) * mm, "end": v(469.13, 190.6) * mm});
            skArc(sketch, "E310", {"start": v(469.13, 190.6) * mm, "mid": v(469.2, 190.4) * mm, "end": v(469.1, 190.2) * mm});
            skLineSegment(sketch, "E311", {"start": v(469.1, 190.2) * mm, "end": v(468.36, 189.46) * mm});
            skArc(sketch, "E312", {"start": v(468.36, 189.46) * mm, "mid": v(468.28, 189.3) * mm, "end": v(468.3, 189.12) * mm});
            skArc(sketch, "E313", {"start": v(468.3, 189.12) * mm, "mid": v(468.62, 187.78) * mm, "end": v(468.3, 186.45) * mm});
            skArc(sketch, "E314", {"start": v(468.3, 186.45) * mm, "mid": v(468.28, 186.26) * mm, "end": v(468.36, 186.1) * mm});
            skLineSegment(sketch, "E315", {"start": v(468.36, 186.1) * mm, "end": v(469.1, 185.36) * mm});
            skArc(sketch, "E316", {"start": v(469.1, 185.36) * mm, "mid": v(469.2, 185.16) * mm, "end": v(469.13, 184.96) * mm});
            skArc(sketch, "E317", {"start": v(469.13, 184.96) * mm, "mid": v(468.8, 184.6) * mm, "end": v(468.44, 184.28) * mm});
            skArc(sketch, "E318", {"start": v(468.44, 184.28) * mm, "mid": v(468.24, 184.21) * mm, "end": v(468.04, 184.3) * mm});
            skLineSegment(sketch, "E319", {"start": v(468.04, 184.3) * mm, "end": v(467.3, 185.04) * mm});
            skArc(sketch, "E320", {"start": v(467.3, 185.04) * mm, "mid": v(467.14, 185.12) * mm, "end": v(466.96, 185.1) * mm});
            skArc(sketch, "E321", {"start": v(466.96, 185.1) * mm, "mid": v(465.62, 184.78) * mm, "end": v(464.28, 185.1) * mm});
            skArc(sketch, "E322", {"start": v(464.28, 185.1) * mm, "mid": v(464.1, 185.12) * mm, "end": v(463.94, 185.04) * mm});
            skLineSegment(sketch, "E323", {"start": v(463.94, 185.04) * mm, "end": v(463.2, 184.3) * mm});
            skArc(sketch, "E324", {"start": v(463.2, 184.3) * mm, "mid": v(463, 184.21) * mm, "end": v(462.8, 184.28) * mm});
            skArc(sketch, "E325", {"start": v(462.8, 184.28) * mm, "mid": v(462.44, 184.6) * mm, "end": v(462.12, 184.96) * mm});
            skArc(sketch, "E326", {"start": v(462.12, 184.96) * mm, "mid": v(462.05, 185.16) * mm, "end": v(462.14, 185.36) * mm});
            skLineSegment(sketch, "E327", {"start": v(462.14, 185.36) * mm, "end": v(462.88, 186.1) * mm});
            skArc(sketch, "E328", {"start": v(462.88, 186.1) * mm, "mid": v(462.96, 186.27) * mm, "end": v(462.93, 186.45) * mm});
            skArc(sketch, "E329", {"start": v(462.93, 186.45) * mm, "mid": v(462.62, 187.78) * mm, "end": v(462.94, 189.12) * mm});
            skArc(sketch, "E330", {"start": v(448.31, 189.12) * mm, "mid": v(448.28, 189.3) * mm, "end": v(448.37, 189.47) * mm});
            skLineSegment(sketch, "E331", {"start": v(448.37, 189.47) * mm, "end": v(449.1, 190.2) * mm});
            skArc(sketch, "E332", {"start": v(449.1, 190.2) * mm, "mid": v(449.2, 190.4) * mm, "end": v(449.13, 190.6) * mm});
            skArc(sketch, "E333", {"start": v(449.13, 190.6) * mm, "mid": v(448.8, 190.97) * mm, "end": v(448.45, 191.29) * mm});
            skArc(sketch, "E334", {"start": v(448.45, 191.29) * mm, "mid": v(448.24, 191.35) * mm, "end": v(448.05, 191.27) * mm});
            skLineSegment(sketch, "E335", {"start": v(448.05, 191.27) * mm, "end": v(447.3, 190.53) * mm});
            skArc(sketch, "E336", {"start": v(447.3, 190.53) * mm, "mid": v(447.14, 190.44) * mm, "end": v(446.96, 190.47) * mm});
            skArc(sketch, "E337", {"start": v(446.96, 190.47) * mm, "mid": v(445.62, 190.78) * mm, "end": v(444.29, 190.47) * mm});
            skArc(sketch, "E338", {"start": v(444.29, 190.47) * mm, "mid": v(444.1, 190.44) * mm, "end": v(443.94, 190.53) * mm});
            skLineSegment(sketch, "E339", {"start": v(443.94, 190.53) * mm, "end": v(443.2, 191.27) * mm});
            skArc(sketch, "E340", {"start": v(443.2, 191.27) * mm, "mid": v(443, 191.35) * mm, "end": v(442.8, 191.29) * mm});
            skArc(sketch, "E341", {"start": v(442.8, 191.29) * mm, "mid": v(442.44, 190.96) * mm, "end": v(442.12, 190.6) * mm});
            skArc(sketch, "E342", {"start": v(442.12, 190.6) * mm, "mid": v(442.05, 190.4) * mm, "end": v(442.14, 190.2) * mm});
            skLineSegment(sketch, "E343", {"start": v(442.14, 190.2) * mm, "end": v(442.88, 189.46) * mm});
            skArc(sketch, "E344", {"start": v(442.88, 189.46) * mm, "mid": v(442.97, 189.3) * mm, "end": v(442.94, 189.12) * mm});
            skArc(sketch, "E345", {"start": v(442.94, 189.12) * mm, "mid": v(442.62, 187.78) * mm, "end": v(442.94, 186.45) * mm});
            skArc(sketch, "E346", {"start": v(442.94, 186.45) * mm, "mid": v(442.97, 186.26) * mm, "end": v(442.88, 186.1) * mm});
            skLineSegment(sketch, "E347", {"start": v(442.88, 186.1) * mm, "end": v(442.14, 185.36) * mm});
            skArc(sketch, "E348", {"start": v(442.14, 185.36) * mm, "mid": v(442.05, 185.16) * mm, "end": v(442.12, 184.96) * mm});
            skArc(sketch, "E349", {"start": v(442.12, 184.96) * mm, "mid": v(442.44, 184.6) * mm, "end": v(442.8, 184.28) * mm});
            skArc(sketch, "E350", {"start": v(442.8, 184.28) * mm, "mid": v(443, 184.21) * mm, "end": v(443.2, 184.3) * mm});
            skLineSegment(sketch, "E351", {"start": v(443.2, 184.3) * mm, "end": v(443.94, 185.04) * mm});
            skArc(sketch, "E352", {"start": v(443.94, 185.04) * mm, "mid": v(444.1, 185.12) * mm, "end": v(444.29, 185.1) * mm});
            skArc(sketch, "E353", {"start": v(444.29, 185.1) * mm, "mid": v(445.63, 184.78) * mm, "end": v(446.96, 185.1) * mm});
            skArc(sketch, "E354", {"start": v(446.96, 185.1) * mm, "mid": v(447.14, 185.12) * mm, "end": v(447.3, 185.04) * mm});
            skLineSegment(sketch, "E355", {"start": v(447.3, 185.04) * mm, "end": v(448.05, 184.3) * mm});
            skArc(sketch, "E356", {"start": v(448.05, 184.3) * mm, "mid": v(448.24, 184.21) * mm, "end": v(448.45, 184.28) * mm});
            skArc(sketch, "E357", {"start": v(448.45, 184.28) * mm, "mid": v(448.8, 184.6) * mm, "end": v(449.13, 184.96) * mm});
            skArc(sketch, "E358", {"start": v(449.13, 184.96) * mm, "mid": v(449.2, 185.16) * mm, "end": v(449.1, 185.36) * mm});
            skLineSegment(sketch, "E359", {"start": v(449.1, 185.36) * mm, "end": v(448.37, 186.1) * mm});
            skArc(sketch, "E360", {"start": v(448.37, 186.1) * mm, "mid": v(448.28, 186.27) * mm, "end": v(448.31, 186.45) * mm});
            skArc(sketch, "E361", {"start": v(448.31, 186.45) * mm, "mid": v(448.62, 187.78) * mm, "end": v(448.31, 189.12) * mm});
            skLineSegment(sketch, "E362", {"start": v(445.62, 189.98) * mm, "end": v(445.63, 185.58) * mm});
            skLineSegment(sketch, "E363", {"start": v(447.82, 187.78) * mm, "end": v(443.42, 187.78) * mm});
            skLineSegment(sketch, "E364", {"start": v(447.82, 207.78) * mm, "end": v(443.42, 207.78) * mm});
            skLineSegment(sketch, "E365", {"start": v(445.62, 205.58) * mm, "end": v(445.62, 209.98) * mm});
            skLineSegment(sketch, "E366", {"start": v(471.08, 197.78) * mm, "end": v(439.4, 197.78) * mm});
            skLineSegment(sketch, "E367", {"start": v(455.62, 181.84) * mm, "end": v(455.62, 213.78) * mm});
            skArc(sketch, "E368", {"start": v(458.86, 199.37) * mm, "mid": v(459.08, 199.54) * mm, "end": v(459.07, 199.82) * mm});
            skArc(sketch, "E369", {"start": v(459.07, 199.82) * mm, "mid": v(458.45, 200.61) * mm, "end": v(457.66, 201.23) * mm});
            skArc(sketch, "E370", {"start": v(457.66, 201.23) * mm, "mid": v(457.38, 201.24) * mm, "end": v(457.21, 201.02) * mm});
            skLineSegment(sketch, "E371", {"start": v(457.21, 201.02) * mm, "end": v(457.08, 200.28) * mm});
            skArc(sketch, "E372", {"start": v(457.08, 200.28) * mm, "mid": v(456.92, 200.07) * mm, "end": v(456.66, 200.06) * mm});
            skArc(sketch, "E373", {"start": v(456.66, 200.06) * mm, "mid": v(455.62, 200.28) * mm, "end": v(454.6, 200.06) * mm});
            skArc(sketch, "E374", {"start": v(454.6, 200.06) * mm, "mid": v(454.33, 200.07) * mm, "end": v(454.17, 200.28) * mm});
            skLineSegment(sketch, "E375", {"start": v(454.17, 200.28) * mm, "end": v(454.04, 201.02) * mm});
            skArc(sketch, "E376", {"start": v(454.04, 201.02) * mm, "mid": v(453.87, 201.24) * mm, "end": v(453.6, 201.23) * mm});
            skArc(sketch, "E377", {"start": v(453.6, 201.23) * mm, "mid": v(452.8, 200.61) * mm, "end": v(452.18, 199.82) * mm});
            skArc(sketch, "E378", {"start": v(452.18, 199.82) * mm, "mid": v(452.17, 199.54) * mm, "end": v(452.39, 199.37) * mm});
            skLineSegment(sketch, "E379", {"start": v(452.39, 199.37) * mm, "end": v(453.13, 199.24) * mm});
            skArc(sketch, "E380", {"start": v(453.13, 199.24) * mm, "mid": v(453.34, 199.08) * mm, "end": v(453.35, 198.82) * mm});
            skArc(sketch, "E381", {"start": v(453.35, 198.82) * mm, "mid": v(453.12, 197.78) * mm, "end": v(453.35, 196.75) * mm});
            skArc(sketch, "E382", {"start": v(453.35, 196.75) * mm, "mid": v(453.34, 196.49) * mm, "end": v(453.13, 196.33) * mm});
            skLineSegment(sketch, "E383", {"start": v(453.13, 196.33) * mm, "end": v(452.39, 196.2) * mm});
            skArc(sketch, "E384", {"start": v(452.39, 196.2) * mm, "mid": v(452.17, 196.03) * mm, "end": v(452.18, 195.75) * mm});
            skArc(sketch, "E385", {"start": v(452.18, 195.75) * mm, "mid": v(452.8, 194.96) * mm, "end": v(453.6, 194.34) * mm});
            skArc(sketch, "E386", {"start": v(453.6, 194.34) * mm, "mid": v(453.87, 194.33) * mm, "end": v(454.04, 194.55) * mm});
            skLineSegment(sketch, "E387", {"start": v(454.04, 194.55) * mm, "end": v(454.17, 195.29) * mm});
            skArc(sketch, "E388", {"start": v(454.17, 195.29) * mm, "mid": v(454.33, 195.5) * mm, "end": v(454.6, 195.5) * mm});
            skArc(sketch, "E389", {"start": v(454.6, 195.5) * mm, "mid": v(455.62, 195.28) * mm, "end": v(456.66, 195.5) * mm});
            skArc(sketch, "E390", {"start": v(456.66, 195.5) * mm, "mid": v(456.92, 195.5) * mm, "end": v(457.08, 195.29) * mm});
            skLineSegment(sketch, "E391", {"start": v(457.08, 195.29) * mm, "end": v(457.21, 194.55) * mm});
            skArc(sketch, "E392", {"start": v(457.21, 194.55) * mm, "mid": v(457.38, 194.33) * mm, "end": v(457.66, 194.34) * mm});
            skArc(sketch, "E393", {"start": v(457.66, 194.34) * mm, "mid": v(458.45, 194.96) * mm, "end": v(459.07, 195.75) * mm});
            skArc(sketch, "E394", {"start": v(459.07, 195.75) * mm, "mid": v(459.08, 196.03) * mm, "end": v(458.86, 196.2) * mm});
            skLineSegment(sketch, "E395", {"start": v(458.86, 196.2) * mm, "end": v(458.12, 196.33) * mm});
            skArc(sketch, "E396", {"start": v(458.12, 196.33) * mm, "mid": v(457.9, 196.49) * mm, "end": v(457.9, 196.75) * mm});
            skArc(sketch, "E397", {"start": v(457.9, 196.75) * mm, "mid": v(458.12, 197.78) * mm, "end": v(457.9, 198.82) * mm});
            skArc(sketch, "E398", {"start": v(457.9, 198.82) * mm, "mid": v(457.9, 199.08) * mm, "end": v(458.12, 199.24) * mm});
            skLineSegment(sketch, "E399", {"start": v(458.12, 199.24) * mm, "end": v(458.86, 199.37) * mm});
            skArc(sketch, "E400", {"start": v(448.31, 206.45) * mm, "mid": v(448.28, 206.27) * mm, "end": v(448.37, 206.1) * mm});
            skLineSegment(sketch, "E401", {"start": v(448.37, 206.1) * mm, "end": v(449.1, 205.36) * mm});
            skArc(sketch, "E402", {"start": v(449.1, 205.36) * mm, "mid": v(449.2, 205.17) * mm, "end": v(449.13, 204.96) * mm});
            skArc(sketch, "E403", {"start": v(449.13, 204.96) * mm, "mid": v(448.8, 204.6) * mm, "end": v(448.45, 204.28) * mm});
            skArc(sketch, "E404", {"start": v(448.45, 204.28) * mm, "mid": v(448.24, 204.21) * mm, "end": v(448.05, 204.3) * mm});
            skLineSegment(sketch, "E405", {"start": v(448.05, 204.3) * mm, "end": v(447.3, 205.04) * mm});
            skArc(sketch, "E406", {"start": v(447.3, 205.04) * mm, "mid": v(447.14, 205.13) * mm, "end": v(446.96, 205.1) * mm});
            skArc(sketch, "E407", {"start": v(446.96, 205.1) * mm, "mid": v(445.62, 204.78) * mm, "end": v(444.29, 205.1) * mm});
            skArc(sketch, "E408", {"start": v(444.29, 205.1) * mm, "mid": v(444.1, 205.13) * mm, "end": v(443.94, 205.04) * mm});
            skLineSegment(sketch, "E409", {"start": v(443.94, 205.04) * mm, "end": v(443.2, 204.3) * mm});
            skArc(sketch, "E410", {"start": v(443.2, 204.3) * mm, "mid": v(443, 204.21) * mm, "end": v(442.8, 204.28) * mm});
            skArc(sketch, "E411", {"start": v(442.8, 204.28) * mm, "mid": v(442.44, 204.6) * mm, "end": v(442.12, 204.96) * mm});
            skArc(sketch, "E412", {"start": v(442.12, 204.96) * mm, "mid": v(442.05, 205.17) * mm, "end": v(442.14, 205.36) * mm});
            skLineSegment(sketch, "E413", {"start": v(442.14, 205.36) * mm, "end": v(442.88, 206.1) * mm});
            skArc(sketch, "E414", {"start": v(442.88, 206.1) * mm, "mid": v(442.97, 206.27) * mm, "end": v(442.94, 206.45) * mm});
            skArc(sketch, "E415", {"start": v(442.94, 206.45) * mm, "mid": v(442.62, 207.78) * mm, "end": v(442.94, 209.12) * mm});
            skArc(sketch, "E416", {"start": v(442.94, 209.12) * mm, "mid": v(442.97, 209.3) * mm, "end": v(442.88, 209.47) * mm});
            skLineSegment(sketch, "E417", {"start": v(442.88, 209.47) * mm, "end": v(442.14, 210.2) * mm});
            skArc(sketch, "E418", {"start": v(442.14, 210.2) * mm, "mid": v(442.05, 210.4) * mm, "end": v(442.12, 210.6) * mm});
            skArc(sketch, "E419", {"start": v(442.12, 210.6) * mm, "mid": v(442.44, 210.97) * mm, "end": v(442.8, 211.29) * mm});
            skArc(sketch, "E420", {"start": v(442.8, 211.29) * mm, "mid": v(443, 211.35) * mm, "end": v(443.2, 211.27) * mm});
            skLineSegment(sketch, "E421", {"start": v(443.2, 211.27) * mm, "end": v(443.94, 210.53) * mm});
            skArc(sketch, "E422", {"start": v(443.94, 210.53) * mm, "mid": v(444.1, 210.44) * mm, "end": v(444.29, 210.47) * mm});
            skArc(sketch, "E423", {"start": v(444.29, 210.47) * mm, "mid": v(445.62, 210.78) * mm, "end": v(446.96, 210.47) * mm});
            skArc(sketch, "E424", {"start": v(446.96, 210.47) * mm, "mid": v(447.14, 210.44) * mm, "end": v(447.3, 210.53) * mm});
            skLineSegment(sketch, "E425", {"start": v(447.3, 210.53) * mm, "end": v(448.05, 211.27) * mm});
            skArc(sketch, "E426", {"start": v(448.05, 211.27) * mm, "mid": v(448.24, 211.35) * mm, "end": v(448.45, 211.29) * mm});
            skArc(sketch, "E427", {"start": v(448.45, 211.29) * mm, "mid": v(448.8, 210.97) * mm, "end": v(449.13, 210.6) * mm});
            skArc(sketch, "E428", {"start": v(449.13, 210.6) * mm, "mid": v(449.2, 210.4) * mm, "end": v(449.1, 210.2) * mm});
            skLineSegment(sketch, "E429", {"start": v(449.1, 210.2) * mm, "end": v(448.37, 209.47) * mm});
            skArc(sketch, "E430", {"start": v(448.37, 209.47) * mm, "mid": v(448.28, 209.3) * mm, "end": v(448.31, 209.12) * mm});
            skArc(sketch, "E431", {"start": v(448.31, 209.12) * mm, "mid": v(448.62, 207.78) * mm, "end": v(448.31, 206.45) * mm});
            skLineSegment(sketch, "E432", {"start": v(459.57, 182.78) * mm, "end": v(458.77, 183.28) * mm});
            skLineSegment(sketch, "E433", {"start": v(458.77, 183.28) * mm, "end": v(458.77, 184.98) * mm});
            skArc(sketch, "E434", {"start": v(458.77, 184.98) * mm, "mid": v(458.86, 185.2) * mm, "end": v(459.07, 185.28) * mm});
            skLineSegment(sketch, "E435", {"start": v(459.07, 185.28) * mm, "end": v(460.72, 185.28) * mm});
            skLineSegment(sketch, "E436", {"start": v(460.72, 185.28) * mm, "end": v(461.71, 188.34) * mm});
            skArc(sketch, "E437", {"start": v(461.71, 188.34) * mm, "mid": v(461.76, 188.6) * mm, "end": v(461.74, 188.86) * mm});
            skArc(sketch, "E438", {"start": v(461.74, 188.86) * mm, "mid": v(460.9, 190.9) * mm, "end": v(459.63, 192.7) * mm});
            skArc(sketch, "E439", {"start": v(459.63, 192.7) * mm, "mid": v(458.78, 193.13) * mm, "end": v(457.84, 193.28) * mm});
            skLineSegment(sketch, "E440", {"start": v(457.84, 193.28) * mm, "end": v(456.12, 193.28) * mm});
            skLineSegment(sketch, "E441", {"start": v(456.12, 193.28) * mm, "end": v(455.62, 193.78) * mm});
            skLineSegment(sketch, "E442", {"start": v(455.62, 193.78) * mm, "end": v(455.12, 193.28) * mm});
            skLineSegment(sketch, "E443", {"start": v(455.12, 193.28) * mm, "end": v(453.4, 193.28) * mm});
            skArc(sketch, "E444", {"start": v(453.4, 193.28) * mm, "mid": v(452.47, 193.13) * mm, "end": v(451.62, 192.7) * mm});
            skArc(sketch, "E445", {"start": v(451.62, 192.7) * mm, "mid": v(450.35, 190.9) * mm, "end": v(449.51, 188.86) * mm});
            skArc(sketch, "E446", {"start": v(449.51, 188.86) * mm, "mid": v(449.49, 188.6) * mm, "end": v(449.54, 188.34) * mm});
            skLineSegment(sketch, "E447", {"start": v(449.54, 188.34) * mm, "end": v(450.52, 185.28) * mm});
            skLineSegment(sketch, "E448", {"start": v(450.52, 185.28) * mm, "end": v(452.17, 185.28) * mm});
            skArc(sketch, "E449", {"start": v(452.17, 185.28) * mm, "mid": v(452.39, 185.2) * mm, "end": v(452.47, 184.98) * mm});
            skLineSegment(sketch, "E450", {"start": v(452.47, 184.98) * mm, "end": v(452.47, 183.28) * mm});
            skLineSegment(sketch, "E451", {"start": v(452.47, 183.28) * mm, "end": v(451.67, 182.78) * mm});
            skLineSegment(sketch, "E452", {"start": v(451.67, 182.78) * mm, "end": v(441.62, 182.78) * mm});
            skArc(sketch, "E453", {"start": v(441.62, 182.78) * mm, "mid": v(440.92, 183.08) * mm, "end": v(440.62, 183.78) * mm});
            skLineSegment(sketch, "E454", {"start": v(440.62, 183.78) * mm, "end": v(440.62, 193.83) * mm});
            skLineSegment(sketch, "E455", {"start": v(440.62, 193.83) * mm, "end": v(441.12, 194.63) * mm});
            skLineSegment(sketch, "E456", {"start": v(441.12, 194.63) * mm, "end": v(442.82, 194.63) * mm});
            skArc(sketch, "E457", {"start": v(442.82, 194.63) * mm, "mid": v(443.04, 194.55) * mm, "end": v(443.12, 194.33) * mm});
            skLineSegment(sketch, "E458", {"start": v(443.12, 194.33) * mm, "end": v(443.12, 192.68) * mm});
            skLineSegment(sketch, "E459", {"start": v(443.12, 192.68) * mm, "end": v(446.18, 191.7) * mm});
            skArc(sketch, "E460", {"start": v(446.18, 191.7) * mm, "mid": v(446.43, 191.65) * mm, "end": v(446.7, 191.67) * mm});
            skArc(sketch, "E461", {"start": v(446.7, 191.67) * mm, "mid": v(448.73, 192.5) * mm, "end": v(450.53, 193.78) * mm});
            skArc(sketch, "E462", {"start": v(450.53, 193.78) * mm, "mid": v(450.97, 194.63) * mm, "end": v(451.12, 195.57) * mm});
            skLineSegment(sketch, "E463", {"start": v(451.12, 195.57) * mm, "end": v(451.12, 197.28) * mm});
            skLineSegment(sketch, "E464", {"start": v(451.12, 197.28) * mm, "end": v(451.62, 197.78) * mm});
            skLineSegment(sketch, "E465", {"start": v(451.62, 197.78) * mm, "end": v(451.12, 198.28) * mm});
            skLineSegment(sketch, "E466", {"start": v(451.12, 198.28) * mm, "end": v(451.12, 200) * mm});
            skArc(sketch, "E467", {"start": v(451.12, 200) * mm, "mid": v(450.97, 200.94) * mm, "end": v(450.53, 201.79) * mm});
            skArc(sketch, "E468", {"start": v(450.53, 201.79) * mm, "mid": v(448.73, 203.06) * mm, "end": v(446.7, 203.9) * mm});
            skArc(sketch, "E469", {"start": v(446.7, 203.9) * mm, "mid": v(446.43, 203.92) * mm, "end": v(446.18, 203.87) * mm});
            skLineSegment(sketch, "E470", {"start": v(446.18, 203.87) * mm, "end": v(443.12, 202.88) * mm});
            skLineSegment(sketch, "E471", {"start": v(443.12, 202.88) * mm, "end": v(443.12, 201.23) * mm});
            skArc(sketch, "E472", {"start": v(443.12, 201.23) * mm, "mid": v(443.04, 201.02) * mm, "end": v(442.82, 200.93) * mm});
            skLineSegment(sketch, "E473", {"start": v(442.82, 200.93) * mm, "end": v(441.12, 200.93) * mm});
            skLineSegment(sketch, "E474", {"start": v(441.12, 200.93) * mm, "end": v(440.62, 201.73) * mm});
            skLineSegment(sketch, "E475", {"start": v(440.62, 201.73) * mm, "end": v(440.62, 211.78) * mm});
            skArc(sketch, "E476", {"start": v(440.62, 211.78) * mm, "mid": v(440.92, 212.5) * mm, "end": v(441.62, 212.78) * mm});
            skLineSegment(sketch, "E477", {"start": v(441.62, 212.78) * mm, "end": v(451.67, 212.78) * mm});
            skLineSegment(sketch, "E478", {"start": v(451.67, 212.78) * mm, "end": v(452.47, 212.28) * mm});
            skLineSegment(sketch, "E479", {"start": v(452.47, 212.28) * mm, "end": v(452.47, 210.58) * mm});
            skArc(sketch, "E480", {"start": v(452.47, 210.58) * mm, "mid": v(452.39, 210.37) * mm, "end": v(452.17, 210.28) * mm});
            skLineSegment(sketch, "E481", {"start": v(452.17, 210.28) * mm, "end": v(450.52, 210.28) * mm});
            skLineSegment(sketch, "E482", {"start": v(450.52, 210.28) * mm, "end": v(449.54, 207.23) * mm});
            skArc(sketch, "E483", {"start": v(449.54, 207.23) * mm, "mid": v(449.49, 206.97) * mm, "end": v(449.51, 206.71) * mm});
            skArc(sketch, "E484", {"start": v(449.51, 206.71) * mm, "mid": v(450.35, 204.67) * mm, "end": v(451.62, 202.87) * mm});
            skArc(sketch, "E485", {"start": v(451.62, 202.87) * mm, "mid": v(452.47, 202.44) * mm, "end": v(453.4, 202.28) * mm});
            skLineSegment(sketch, "E486", {"start": v(453.4, 202.28) * mm, "end": v(455.12, 202.28) * mm});
            skLineSegment(sketch, "E487", {"start": v(455.12, 202.28) * mm, "end": v(455.62, 201.78) * mm});
            skLineSegment(sketch, "E488", {"start": v(455.62, 201.78) * mm, "end": v(456.12, 202.28) * mm});
            skLineSegment(sketch, "E489", {"start": v(456.12, 202.28) * mm, "end": v(457.84, 202.28) * mm});
            skArc(sketch, "E490", {"start": v(457.84, 202.28) * mm, "mid": v(458.78, 202.44) * mm, "end": v(459.63, 202.87) * mm});
            skArc(sketch, "E491", {"start": v(459.63, 202.87) * mm, "mid": v(460.9, 204.67) * mm, "end": v(461.74, 206.71) * mm});
            skArc(sketch, "E492", {"start": v(461.74, 206.71) * mm, "mid": v(461.76, 206.97) * mm, "end": v(461.71, 207.23) * mm});
            skLineSegment(sketch, "E493", {"start": v(461.71, 207.23) * mm, "end": v(460.72, 210.28) * mm});
            skLineSegment(sketch, "E494", {"start": v(460.72, 210.28) * mm, "end": v(459.07, 210.28) * mm});
            skArc(sketch, "E495", {"start": v(459.07, 210.28) * mm, "mid": v(458.86, 210.37) * mm, "end": v(458.77, 210.58) * mm});
            skLineSegment(sketch, "E496", {"start": v(458.77, 210.58) * mm, "end": v(458.77, 212.28) * mm});
            skLineSegment(sketch, "E497", {"start": v(458.77, 212.28) * mm, "end": v(459.57, 212.78) * mm});
            skLineSegment(sketch, "E498", {"start": v(459.57, 212.78) * mm, "end": v(469.62, 212.78) * mm});
            skArc(sketch, "E499", {"start": v(469.62, 212.78) * mm, "mid": v(470.33, 212.5) * mm, "end": v(470.62, 211.78) * mm});
            skLineSegment(sketch, "E500", {"start": v(470.62, 211.78) * mm, "end": v(470.62, 201.73) * mm});
            skLineSegment(sketch, "E501", {"start": v(470.62, 201.73) * mm, "end": v(470.12, 200.93) * mm});
            skLineSegment(sketch, "E502", {"start": v(470.12, 200.93) * mm, "end": v(468.42, 200.93) * mm});
            skArc(sketch, "E503", {"start": v(468.42, 200.93) * mm, "mid": v(468.21, 201.02) * mm, "end": v(468.12, 201.23) * mm});
            skLineSegment(sketch, "E504", {"start": v(468.12, 201.23) * mm, "end": v(468.12, 202.88) * mm});
            skLineSegment(sketch, "E505", {"start": v(468.12, 202.88) * mm, "end": v(465.07, 203.87) * mm});
            skArc(sketch, "E506", {"start": v(465.07, 203.87) * mm, "mid": v(464.81, 203.92) * mm, "end": v(464.55, 203.9) * mm});
            skArc(sketch, "E507", {"start": v(464.55, 203.9) * mm, "mid": v(462.51, 203.06) * mm, "end": v(460.71, 201.79) * mm});
            skArc(sketch, "E508", {"start": v(460.71, 201.79) * mm, "mid": v(460.28, 200.94) * mm, "end": v(460.12, 200) * mm});
            skLineSegment(sketch, "E509", {"start": v(460.12, 200) * mm, "end": v(460.12, 198.28) * mm});
            skLineSegment(sketch, "E510", {"start": v(460.12, 198.28) * mm, "end": v(459.62, 197.78) * mm});
            skLineSegment(sketch, "E511", {"start": v(459.62, 197.78) * mm, "end": v(460.12, 197.28) * mm});
            skLineSegment(sketch, "E512", {"start": v(460.12, 197.28) * mm, "end": v(460.12, 195.57) * mm});
            skArc(sketch, "E513", {"start": v(460.12, 195.57) * mm, "mid": v(460.28, 194.63) * mm, "end": v(460.71, 193.78) * mm});
            skArc(sketch, "E514", {"start": v(460.71, 193.78) * mm, "mid": v(462.51, 192.5) * mm, "end": v(464.55, 191.67) * mm});
            skArc(sketch, "E515", {"start": v(464.55, 191.67) * mm, "mid": v(464.81, 191.65) * mm, "end": v(465.07, 191.7) * mm});
            skLineSegment(sketch, "E516", {"start": v(465.07, 191.7) * mm, "end": v(468.12, 192.68) * mm});
            skLineSegment(sketch, "E517", {"start": v(468.12, 192.68) * mm, "end": v(468.12, 194.33) * mm});
            skArc(sketch, "E518", {"start": v(468.12, 194.33) * mm, "mid": v(468.21, 194.55) * mm, "end": v(468.42, 194.63) * mm});
            skLineSegment(sketch, "E519", {"start": v(468.42, 194.63) * mm, "end": v(470.12, 194.63) * mm});
            skLineSegment(sketch, "E520", {"start": v(470.12, 194.63) * mm, "end": v(470.62, 193.83) * mm});
            skLineSegment(sketch, "E521", {"start": v(470.62, 193.83) * mm, "end": v(470.62, 183.78) * mm});
            skArc(sketch, "E522", {"start": v(470.62, 183.78) * mm, "mid": v(470.33, 183.08) * mm, "end": v(469.62, 182.78) * mm});
            skLineSegment(sketch, "E523", {"start": v(469.62, 182.78) * mm, "end": v(459.57, 182.78) * mm});
            skLineSegment(sketch, "E524", {"start": v(-2.82, -20.25) * mm, "end": v(-2.82, -15.85) * mm});
            skLineSegment(sketch, "E525", {"start": v(-5.02, -18.05) * mm, "end": v(-0.62, -18.05) * mm});
            skArc(sketch, "E526", {"start": v(-5.5, -19.39) * mm, "mid": v(-5.48, -19.57) * mm, "end": v(-5.56, -19.74) * mm});
            skLineSegment(sketch, "E527", {"start": v(-5.56, -19.74) * mm, "end": v(-6.3, -20.48) * mm});
            skArc(sketch, "E528", {"start": v(-6.3, -20.48) * mm, "mid": v(-6.4, -20.67) * mm, "end": v(-6.32, -20.88) * mm});
            skArc(sketch, "E529", {"start": v(-6.32, -20.88) * mm, "mid": v(-6, -21.24) * mm, "end": v(-5.64, -21.56) * mm});
            skArc(sketch, "E530", {"start": v(-5.64, -21.56) * mm, "mid": v(-5.44, -21.62) * mm, "end": v(-5.24, -21.54) * mm});
            skLineSegment(sketch, "E531", {"start": v(-5.24, -21.54) * mm, "end": v(-4.5, -20.8) * mm});
            skArc(sketch, "E532", {"start": v(-4.5, -20.8) * mm, "mid": v(-4.34, -20.71) * mm, "end": v(-4.16, -20.74) * mm});
            skArc(sketch, "E533", {"start": v(-4.16, -20.74) * mm, "mid": v(-2.82, -21.05) * mm, "end": v(-1.48, -20.74) * mm});
            skArc(sketch, "E534", {"start": v(-1.48, -20.74) * mm, "mid": v(-1.3, -20.71) * mm, "end": v(-1.14, -20.8) * mm});
            skLineSegment(sketch, "E535", {"start": v(-1.14, -20.8) * mm, "end": v(-0.4, -21.54) * mm});
            skArc(sketch, "E536", {"start": v(-0.4, -21.54) * mm, "mid": v(-0.2, -21.62) * mm, "end": v(0, -21.56) * mm});
            skArc(sketch, "E537", {"start": v(0, -21.56) * mm, "mid": v(0.36, -21.24) * mm, "end": v(0.68, -20.88) * mm});
            skArc(sketch, "E538", {"start": v(0.68, -20.88) * mm, "mid": v(0.75, -20.67) * mm, "end": v(0.66, -20.48) * mm});
            skLineSegment(sketch, "E539", {"start": v(0.66, -20.48) * mm, "end": v(-0.08, -19.74) * mm});
            skArc(sketch, "E540", {"start": v(-0.08, -19.74) * mm, "mid": v(-0.16, -19.57) * mm, "end": v(-0.13, -19.39) * mm});
            skArc(sketch, "E541", {"start": v(-0.13, -19.39) * mm, "mid": v(0.18, -18.05) * mm, "end": v(-0.13, -16.72) * mm});
            skArc(sketch, "E542", {"start": v(-0.13, -16.72) * mm, "mid": v(-0.16, -16.54) * mm, "end": v(-0.08, -16.37) * mm});
            skLineSegment(sketch, "E543", {"start": v(-0.08, -16.37) * mm, "end": v(0.66, -15.63) * mm});
            skArc(sketch, "E544", {"start": v(0.66, -15.63) * mm, "mid": v(0.75, -15.44) * mm, "end": v(0.68, -15.23) * mm});
            skArc(sketch, "E545", {"start": v(0.68, -15.23) * mm, "mid": v(0.36, -14.87) * mm, "end": v(0, -14.55) * mm});
            skArc(sketch, "E546", {"start": v(0, -14.55) * mm, "mid": v(-0.2, -14.48) * mm, "end": v(-0.4, -14.57) * mm});
            skLineSegment(sketch, "E547", {"start": v(-0.4, -14.57) * mm, "end": v(-1.14, -15.31) * mm});
            skArc(sketch, "E548", {"start": v(-1.14, -15.31) * mm, "mid": v(-1.3, -15.4) * mm, "end": v(-1.48, -15.37) * mm});
            skArc(sketch, "E549", {"start": v(-1.48, -15.37) * mm, "mid": v(-2.82, -15.05) * mm, "end": v(-4.16, -15.37) * mm});
            skArc(sketch, "E550", {"start": v(-4.16, -15.37) * mm, "mid": v(-4.34, -15.4) * mm, "end": v(-4.5, -15.31) * mm});
            skLineSegment(sketch, "E551", {"start": v(-4.5, -15.31) * mm, "end": v(-5.24, -14.57) * mm});
            skArc(sketch, "E552", {"start": v(-5.24, -14.57) * mm, "mid": v(-5.44, -14.48) * mm, "end": v(-5.64, -14.55) * mm});
            skArc(sketch, "E553", {"start": v(-5.64, -14.55) * mm, "mid": v(-6, -14.87) * mm, "end": v(-6.32, -15.23) * mm});
            skArc(sketch, "E554", {"start": v(-6.32, -15.23) * mm, "mid": v(-6.4, -15.44) * mm, "end": v(-6.3, -15.63) * mm});
            skLineSegment(sketch, "E555", {"start": v(-6.3, -15.63) * mm, "end": v(-5.56, -16.37) * mm});
            skArc(sketch, "E556", {"start": v(-5.56, -16.37) * mm, "mid": v(-5.48, -16.54) * mm, "end": v(-5.5, -16.72) * mm});
            skArc(sketch, "E557", {"start": v(-5.5, -16.72) * mm, "mid": v(-5.82, -18.05) * mm, "end": v(-5.5, -19.39) * mm});
            skLineSegment(sketch, "E558", {"start": v(-5.02, -38.05) * mm, "end": v(-0.62, -38.05) * mm});
            skLineSegment(sketch, "E559", {"start": v(-2.82, -35.85) * mm, "end": v(-2.82, -40.25) * mm});
            skArc(sketch, "E560", {"start": v(-5.5, -36.72) * mm, "mid": v(-5.48, -36.54) * mm, "end": v(-5.56, -36.37) * mm});
            skLineSegment(sketch, "E561", {"start": v(-5.56, -36.37) * mm, "end": v(-6.3, -35.63) * mm});
            skArc(sketch, "E562", {"start": v(-6.3, -35.63) * mm, "mid": v(-6.4, -35.44) * mm, "end": v(-6.33, -35.23) * mm});
            skArc(sketch, "E563", {"start": v(-6.33, -35.23) * mm, "mid": v(-6, -34.87) * mm, "end": v(-5.64, -34.55) * mm});
            skArc(sketch, "E564", {"start": v(-5.64, -34.55) * mm, "mid": v(-5.44, -34.48) * mm, "end": v(-5.24, -34.57) * mm});
            skLineSegment(sketch, "E565", {"start": v(-5.24, -34.57) * mm, "end": v(-4.5, -35.31) * mm});
            skArc(sketch, "E566", {"start": v(-4.5, -35.31) * mm, "mid": v(-4.34, -35.4) * mm, "end": v(-4.16, -35.37) * mm});
            skArc(sketch, "E567", {"start": v(-4.16, -35.37) * mm, "mid": v(-2.82, -35.05) * mm, "end": v(-1.48, -35.37) * mm});
            skArc(sketch, "E568", {"start": v(-1.48, -35.37) * mm, "mid": v(-1.3, -35.4) * mm, "end": v(-1.14, -35.31) * mm});
            skLineSegment(sketch, "E569", {"start": v(-1.14, -35.31) * mm, "end": v(-0.4, -34.57) * mm});
            skArc(sketch, "E570", {"start": v(-0.4, -34.57) * mm, "mid": v(-0.2, -34.48) * mm, "end": v(0, -34.55) * mm});
            skArc(sketch, "E571", {"start": v(0, -34.55) * mm, "mid": v(0.36, -34.87) * mm, "end": v(0.68, -35.23) * mm});
            skArc(sketch, "E572", {"start": v(0.68, -35.23) * mm, "mid": v(0.75, -35.44) * mm, "end": v(0.66, -35.63) * mm});
            skLineSegment(sketch, "E573", {"start": v(0.66, -35.63) * mm, "end": v(-0.08, -36.37) * mm});
            skArc(sketch, "E574", {"start": v(-0.08, -36.37) * mm, "mid": v(-0.16, -36.54) * mm, "end": v(-0.13, -36.72) * mm});
            skArc(sketch, "E575", {"start": v(-0.13, -36.72) * mm, "mid": v(0.18, -38.05) * mm, "end": v(-0.14, -39.4) * mm});
            skArc(sketch, "E576", {"start": v(-0.14, -39.4) * mm, "mid": v(-0.16, -39.57) * mm, "end": v(-0.08, -39.74) * mm});
            skLineSegment(sketch, "E577", {"start": v(-0.08, -39.74) * mm, "end": v(0.66, -40.48) * mm});
            skArc(sketch, "E578", {"start": v(0.66, -40.48) * mm, "mid": v(0.75, -40.67) * mm, "end": v(0.68, -40.88) * mm});
            skArc(sketch, "E579", {"start": v(0.68, -40.88) * mm, "mid": v(0.36, -41.24) * mm, "end": v(0, -41.56) * mm});
            skArc(sketch, "E580", {"start": v(0, -41.56) * mm, "mid": v(-0.2, -41.63) * mm, "end": v(-0.4, -41.54) * mm});
            skLineSegment(sketch, "E581", {"start": v(-0.4, -41.54) * mm, "end": v(-1.14, -40.8) * mm});
            skArc(sketch, "E582", {"start": v(-1.14, -40.8) * mm, "mid": v(-1.3, -40.71) * mm, "end": v(-1.49, -40.74) * mm});
            skArc(sketch, "E583", {"start": v(-1.49, -40.74) * mm, "mid": v(-2.82, -41.05) * mm, "end": v(-4.16, -40.74) * mm});
            skArc(sketch, "E584", {"start": v(-4.16, -40.74) * mm, "mid": v(-4.34, -40.71) * mm, "end": v(-4.5, -40.8) * mm});
            skLineSegment(sketch, "E585", {"start": v(-4.5, -40.8) * mm, "end": v(-5.24, -41.54) * mm});
            skArc(sketch, "E586", {"start": v(-5.24, -41.54) * mm, "mid": v(-5.44, -41.62) * mm, "end": v(-5.64, -41.56) * mm});
            skArc(sketch, "E587", {"start": v(-5.64, -41.56) * mm, "mid": v(-6, -41.24) * mm, "end": v(-6.33, -40.88) * mm});
            skArc(sketch, "E588", {"start": v(-6.33, -40.88) * mm, "mid": v(-6.4, -40.67) * mm, "end": v(-6.3, -40.48) * mm});
            skLineSegment(sketch, "E589", {"start": v(-6.3, -40.48) * mm, "end": v(-5.56, -39.74) * mm});
            skArc(sketch, "E590", {"start": v(-5.56, -39.74) * mm, "mid": v(-5.48, -39.57) * mm, "end": v(-5.5, -39.4) * mm});
            skArc(sketch, "E591", {"start": v(-5.5, -39.4) * mm, "mid": v(-5.82, -38.05) * mm, "end": v(-5.5, -36.72) * mm});
            skArc(sketch, "E592", {"start": v(-20.13, -36.72) * mm, "mid": v(-20.16, -36.54) * mm, "end": v(-20.07, -36.37) * mm});
            skLineSegment(sketch, "E593", {"start": v(-20.07, -36.37) * mm, "end": v(-19.33, -35.63) * mm});
            skArc(sketch, "E594", {"start": v(-19.33, -35.63) * mm, "mid": v(-19.25, -35.44) * mm, "end": v(-19.31, -35.23) * mm});
            skArc(sketch, "E595", {"start": v(-19.31, -35.23) * mm, "mid": v(-19.64, -34.87) * mm, "end": v(-20, -34.55) * mm});
            skArc(sketch, "E596", {"start": v(-20, -34.55) * mm, "mid": v(-20.2, -34.48) * mm, "end": v(-20.4, -34.57) * mm});
            skLineSegment(sketch, "E597", {"start": v(-20.4, -34.57) * mm, "end": v(-21.14, -35.31) * mm});
            skArc(sketch, "E598", {"start": v(-21.14, -35.31) * mm, "mid": v(-21.3, -35.4) * mm, "end": v(-21.48, -35.37) * mm});
            skArc(sketch, "E599", {"start": v(-21.48, -35.37) * mm, "mid": v(-22.82, -35.05) * mm, "end": v(-24.15, -35.37) * mm});
            skArc(sketch, "E600", {"start": v(-24.15, -35.37) * mm, "mid": v(-24.34, -35.4) * mm, "end": v(-24.5, -35.31) * mm});
            skLineSegment(sketch, "E601", {"start": v(-24.5, -35.31) * mm, "end": v(-25.24, -34.57) * mm});
            skArc(sketch, "E602", {"start": v(-25.24, -34.57) * mm, "mid": v(-25.44, -34.48) * mm, "end": v(-25.64, -34.55) * mm});
            skArc(sketch, "E603", {"start": v(-25.64, -34.55) * mm, "mid": v(-26, -34.87) * mm, "end": v(-26.32, -35.23) * mm});
            skArc(sketch, "E604", {"start": v(-26.32, -35.23) * mm, "mid": v(-26.39, -35.44) * mm, "end": v(-26.3, -35.63) * mm});
            skLineSegment(sketch, "E605", {"start": v(-26.3, -35.63) * mm, "end": v(-25.56, -36.37) * mm});
            skArc(sketch, "E606", {"start": v(-25.56, -36.37) * mm, "mid": v(-25.48, -36.54) * mm, "end": v(-25.5, -36.72) * mm});
            skArc(sketch, "E607", {"start": v(-25.5, -36.72) * mm, "mid": v(-25.82, -38.05) * mm, "end": v(-25.5, -39.4) * mm});
            skArc(sketch, "E608", {"start": v(-25.5, -39.4) * mm, "mid": v(-25.48, -39.57) * mm, "end": v(-25.56, -39.74) * mm});
            skLineSegment(sketch, "E609", {"start": v(-25.56, -39.74) * mm, "end": v(-26.3, -40.48) * mm});
            skArc(sketch, "E610", {"start": v(-26.3, -40.48) * mm, "mid": v(-26.39, -40.67) * mm, "end": v(-26.32, -40.88) * mm});
            skArc(sketch, "E611", {"start": v(-26.32, -40.88) * mm, "mid": v(-26, -41.24) * mm, "end": v(-25.64, -41.56) * mm});
            skArc(sketch, "E612", {"start": v(-25.64, -41.56) * mm, "mid": v(-25.44, -41.63) * mm, "end": v(-25.24, -41.54) * mm});
            skLineSegment(sketch, "E613", {"start": v(-25.24, -41.54) * mm, "end": v(-24.5, -40.8) * mm});
            skArc(sketch, "E614", {"start": v(-24.5, -40.8) * mm, "mid": v(-24.33, -40.71) * mm, "end": v(-24.15, -40.74) * mm});
            skArc(sketch, "E615", {"start": v(-24.15, -40.74) * mm, "mid": v(-22.82, -41.05) * mm, "end": v(-21.48, -40.74) * mm});
            skArc(sketch, "E616", {"start": v(-21.48, -40.74) * mm, "mid": v(-21.3, -40.71) * mm, "end": v(-21.14, -40.8) * mm});
            skLineSegment(sketch, "E617", {"start": v(-21.14, -40.8) * mm, "end": v(-20.4, -41.54) * mm});
            skArc(sketch, "E618", {"start": v(-20.4, -41.54) * mm, "mid": v(-20.2, -41.62) * mm, "end": v(-20, -41.56) * mm});
            skArc(sketch, "E619", {"start": v(-20, -41.56) * mm, "mid": v(-19.63, -41.24) * mm, "end": v(-19.31, -40.88) * mm});
            skArc(sketch, "E620", {"start": v(-19.31, -40.88) * mm, "mid": v(-19.25, -40.67) * mm, "end": v(-19.33, -40.48) * mm});
            skLineSegment(sketch, "E621", {"start": v(-19.33, -40.48) * mm, "end": v(-20.07, -39.74) * mm});
            skArc(sketch, "E622", {"start": v(-20.07, -39.74) * mm, "mid": v(-20.16, -39.57) * mm, "end": v(-20.13, -39.4) * mm});
            skArc(sketch, "E623", {"start": v(-20.13, -39.4) * mm, "mid": v(-19.82, -38.05) * mm, "end": v(-20.13, -36.72) * mm});
            skLineSegment(sketch, "E624", {"start": v(-22.82, -35.85) * mm, "end": v(-22.82, -40.25) * mm});
            skLineSegment(sketch, "E625", {"start": v(-20.62, -38.05) * mm, "end": v(-25.02, -38.05) * mm});
            skLineSegment(sketch, "E626", {"start": v(-20.62, -18.05) * mm, "end": v(-25.02, -18.05) * mm});
            skLineSegment(sketch, "E627", {"start": v(-22.82, -20.25) * mm, "end": v(-22.82, -15.85) * mm});
            skLineSegment(sketch, "E628", {"start": v(2.64, -28.05) * mm, "end": v(-29.04, -28.05) * mm});
            skLineSegment(sketch, "E629", {"start": v(-12.82, -44) * mm, "end": v(-12.82, -12.06) * mm});
            skArc(sketch, "E630", {"start": v(-9.58, -26.47) * mm, "mid": v(-9.36, -26.3) * mm, "end": v(-9.38, -26.02) * mm});
            skArc(sketch, "E631", {"start": v(-9.38, -26.02) * mm, "mid": v(-10, -25.23) * mm, "end": v(-10.78, -24.61) * mm});
            skArc(sketch, "E632", {"start": v(-10.78, -24.61) * mm, "mid": v(-11.06, -24.6) * mm, "end": v(-11.23, -24.82) * mm});
            skLineSegment(sketch, "E633", {"start": v(-11.23, -24.82) * mm, "end": v(-11.37, -25.56) * mm});
            skArc(sketch, "E634", {"start": v(-11.37, -25.56) * mm, "mid": v(-11.52, -25.77) * mm, "end": v(-11.78, -25.78) * mm});
            skArc(sketch, "E635", {"start": v(-11.78, -25.78) * mm, "mid": v(-12.82, -25.55) * mm, "end": v(-13.85, -25.78) * mm});
            skArc(sketch, "E636", {"start": v(-13.85, -25.78) * mm, "mid": v(-14.11, -25.77) * mm, "end": v(-14.27, -25.56) * mm});
            skLineSegment(sketch, "E637", {"start": v(-14.27, -25.56) * mm, "end": v(-14.4, -24.82) * mm});
            skArc(sketch, "E638", {"start": v(-14.4, -24.82) * mm, "mid": v(-14.57, -24.6) * mm, "end": v(-14.85, -24.61) * mm});
            skArc(sketch, "E639", {"start": v(-14.85, -24.61) * mm, "mid": v(-15.65, -25.23) * mm, "end": v(-16.26, -26.02) * mm});
            skArc(sketch, "E640", {"start": v(-16.26, -26.02) * mm, "mid": v(-16.27, -26.3) * mm, "end": v(-16.06, -26.47) * mm});
            skLineSegment(sketch, "E641", {"start": v(-16.06, -26.47) * mm, "end": v(-15.31, -26.6) * mm});
            skArc(sketch, "E642", {"start": v(-15.31, -26.6) * mm, "mid": v(-15.1, -26.76) * mm, "end": v(-15.1, -27.02) * mm});
            skArc(sketch, "E643", {"start": v(-15.1, -27.02) * mm, "mid": v(-15.32, -28.05) * mm, "end": v(-15.1, -29.09) * mm});
            skArc(sketch, "E644", {"start": v(-15.1, -29.09) * mm, "mid": v(-15.1, -29.35) * mm, "end": v(-15.31, -29.5) * mm});
            skLineSegment(sketch, "E645", {"start": v(-15.31, -29.5) * mm, "end": v(-16.06, -29.64) * mm});
            skArc(sketch, "E646", {"start": v(-16.06, -29.64) * mm, "mid": v(-16.27, -29.81) * mm, "end": v(-16.26, -30.09) * mm});
            skArc(sketch, "E647", {"start": v(-16.26, -30.09) * mm, "mid": v(-15.65, -30.88) * mm, "end": v(-14.85, -31.5) * mm});
            skArc(sketch, "E648", {"start": v(-14.85, -31.5) * mm, "mid": v(-14.57, -31.51) * mm, "end": v(-14.4, -31.3) * mm});
            skLineSegment(sketch, "E649", {"start": v(-14.4, -31.3) * mm, "end": v(-14.27, -30.55) * mm});
            skArc(sketch, "E650", {"start": v(-14.27, -30.55) * mm, "mid": v(-14.11, -30.34) * mm, "end": v(-13.85, -30.33) * mm});
            skArc(sketch, "E651", {"start": v(-13.85, -30.33) * mm, "mid": v(-12.82, -30.55) * mm, "end": v(-11.78, -30.33) * mm});
            skArc(sketch, "E652", {"start": v(-11.78, -30.33) * mm, "mid": v(-11.52, -30.34) * mm, "end": v(-11.37, -30.55) * mm});
            skLineSegment(sketch, "E653", {"start": v(-11.37, -30.55) * mm, "end": v(-11.23, -31.3) * mm});
            skArc(sketch, "E654", {"start": v(-11.23, -31.3) * mm, "mid": v(-11.06, -31.51) * mm, "end": v(-10.78, -31.5) * mm});
            skArc(sketch, "E655", {"start": v(-10.78, -31.5) * mm, "mid": v(-10, -30.88) * mm, "end": v(-9.38, -30.09) * mm});
            skArc(sketch, "E656", {"start": v(-9.38, -30.09) * mm, "mid": v(-9.36, -29.81) * mm, "end": v(-9.58, -29.64) * mm});
            skLineSegment(sketch, "E657", {"start": v(-9.58, -29.64) * mm, "end": v(-10.32, -29.5) * mm});
            skArc(sketch, "E658", {"start": v(-10.32, -29.5) * mm, "mid": v(-10.53, -29.35) * mm, "end": v(-10.54, -29.09) * mm});
            skArc(sketch, "E659", {"start": v(-10.54, -29.09) * mm, "mid": v(-10.32, -28.05) * mm, "end": v(-10.54, -27.02) * mm});
            skArc(sketch, "E660", {"start": v(-10.54, -27.02) * mm, "mid": v(-10.53, -26.76) * mm, "end": v(-10.32, -26.6) * mm});
            skLineSegment(sketch, "E661", {"start": v(-10.32, -26.6) * mm, "end": v(-9.58, -26.47) * mm});
            skArc(sketch, "E662", {"start": v(-20.13, -19.39) * mm, "mid": v(-20.16, -19.57) * mm, "end": v(-20.08, -19.74) * mm});
            skLineSegment(sketch, "E663", {"start": v(-20.08, -19.74) * mm, "end": v(-19.33, -20.48) * mm});
            skArc(sketch, "E664", {"start": v(-19.33, -20.48) * mm, "mid": v(-19.25, -20.67) * mm, "end": v(-19.31, -20.88) * mm});
            skArc(sketch, "E665", {"start": v(-19.31, -20.88) * mm, "mid": v(-19.64, -21.24) * mm, "end": v(-20, -21.56) * mm});
            skArc(sketch, "E666", {"start": v(-20, -21.56) * mm, "mid": v(-20.2, -21.62) * mm, "end": v(-20.4, -21.54) * mm});
            skLineSegment(sketch, "E667", {"start": v(-20.4, -21.54) * mm, "end": v(-21.14, -20.8) * mm});
            skArc(sketch, "E668", {"start": v(-21.14, -20.8) * mm, "mid": v(-21.3, -20.71) * mm, "end": v(-21.48, -20.74) * mm});
            skArc(sketch, "E669", {"start": v(-21.48, -20.74) * mm, "mid": v(-22.82, -21.05) * mm, "end": v(-24.15, -20.74) * mm});
            skArc(sketch, "E670", {"start": v(-24.15, -20.74) * mm, "mid": v(-24.34, -20.71) * mm, "end": v(-24.5, -20.8) * mm});
            skLineSegment(sketch, "E671", {"start": v(-24.5, -20.8) * mm, "end": v(-25.24, -21.54) * mm});
            skArc(sketch, "E672", {"start": v(-25.24, -21.54) * mm, "mid": v(-25.44, -21.62) * mm, "end": v(-25.64, -21.56) * mm});
            skArc(sketch, "E673", {"start": v(-25.64, -21.56) * mm, "mid": v(-26, -21.24) * mm, "end": v(-26.32, -20.88) * mm});
            skArc(sketch, "E674", {"start": v(-26.32, -20.88) * mm, "mid": v(-26.39, -20.67) * mm, "end": v(-26.3, -20.48) * mm});
            skLineSegment(sketch, "E675", {"start": v(-26.3, -20.48) * mm, "end": v(-25.56, -19.74) * mm});
            skArc(sketch, "E676", {"start": v(-25.56, -19.74) * mm, "mid": v(-25.48, -19.57) * mm, "end": v(-25.5, -19.39) * mm});
            skArc(sketch, "E677", {"start": v(-25.5, -19.39) * mm, "mid": v(-25.82, -18.05) * mm, "end": v(-25.5, -16.72) * mm});
            skArc(sketch, "E678", {"start": v(-25.5, -16.72) * mm, "mid": v(-25.48, -16.54) * mm, "end": v(-25.56, -16.37) * mm});
            skLineSegment(sketch, "E679", {"start": v(-25.56, -16.37) * mm, "end": v(-26.3, -15.63) * mm});
            skArc(sketch, "E680", {"start": v(-26.3, -15.63) * mm, "mid": v(-26.39, -15.44) * mm, "end": v(-26.32, -15.23) * mm});
            skArc(sketch, "E681", {"start": v(-26.32, -15.23) * mm, "mid": v(-26, -14.87) * mm, "end": v(-25.64, -14.55) * mm});
            skArc(sketch, "E682", {"start": v(-25.64, -14.55) * mm, "mid": v(-25.44, -14.48) * mm, "end": v(-25.24, -14.57) * mm});
            skLineSegment(sketch, "E683", {"start": v(-25.24, -14.57) * mm, "end": v(-24.5, -15.31) * mm});
            skArc(sketch, "E684", {"start": v(-24.5, -15.31) * mm, "mid": v(-24.34, -15.4) * mm, "end": v(-24.15, -15.37) * mm});
            skArc(sketch, "E685", {"start": v(-24.15, -15.37) * mm, "mid": v(-22.82, -15.05) * mm, "end": v(-21.48, -15.37) * mm});
            skArc(sketch, "E686", {"start": v(-21.48, -15.37) * mm, "mid": v(-21.3, -15.4) * mm, "end": v(-21.14, -15.31) * mm});
            skLineSegment(sketch, "E687", {"start": v(-21.14, -15.31) * mm, "end": v(-20.4, -14.57) * mm});
            skArc(sketch, "E688", {"start": v(-20.4, -14.57) * mm, "mid": v(-20.2, -14.48) * mm, "end": v(-20, -14.55) * mm});
            skArc(sketch, "E689", {"start": v(-20, -14.55) * mm, "mid": v(-19.64, -14.87) * mm, "end": v(-19.31, -15.23) * mm});
            skArc(sketch, "E690", {"start": v(-19.31, -15.23) * mm, "mid": v(-19.25, -15.44) * mm, "end": v(-19.33, -15.63) * mm});
            skLineSegment(sketch, "E691", {"start": v(-19.33, -15.63) * mm, "end": v(-20.08, -16.37) * mm});
            skArc(sketch, "E692", {"start": v(-20.08, -16.37) * mm, "mid": v(-20.16, -16.54) * mm, "end": v(-20.13, -16.72) * mm});
            skArc(sketch, "E693", {"start": v(-20.13, -16.72) * mm, "mid": v(-19.82, -18.05) * mm, "end": v(-20.13, -19.39) * mm});
            skLineSegment(sketch, "E694", {"start": v(-8.87, -43.05) * mm, "end": v(-9.67, -42.55) * mm});
            skLineSegment(sketch, "E695", {"start": v(-9.67, -42.55) * mm, "end": v(-9.67, -40.85) * mm});
            skArc(sketch, "E696", {"start": v(-9.67, -40.85) * mm, "mid": v(-9.58, -40.64) * mm, "end": v(-9.37, -40.55) * mm});
            skLineSegment(sketch, "E697", {"start": v(-9.37, -40.55) * mm, "end": v(-7.72, -40.55) * mm});
            skLineSegment(sketch, "E698", {"start": v(-7.72, -40.55) * mm, "end": v(-6.73, -37.5) * mm});
            skArc(sketch, "E699", {"start": v(-6.73, -37.5) * mm, "mid": v(-6.68, -37.24) * mm, "end": v(-6.7, -36.98) * mm});
            skArc(sketch, "E700", {"start": v(-6.7, -36.98) * mm, "mid": v(-7.54, -34.94) * mm, "end": v(-8.81, -33.14) * mm});
            skArc(sketch, "E701", {"start": v(-8.81, -33.14) * mm, "mid": v(-9.66, -32.7) * mm, "end": v(-10.6, -32.55) * mm});
            skLineSegment(sketch, "E702", {"start": v(-10.6, -32.55) * mm, "end": v(-12.32, -32.55) * mm});
            skLineSegment(sketch, "E703", {"start": v(-12.32, -32.55) * mm, "end": v(-12.82, -32.05) * mm});
            skLineSegment(sketch, "E704", {"start": v(-12.82, -32.05) * mm, "end": v(-13.32, -32.55) * mm});
            skLineSegment(sketch, "E705", {"start": v(-13.32, -32.55) * mm, "end": v(-15.04, -32.55) * mm});
            skArc(sketch, "E706", {"start": v(-15.04, -32.55) * mm, "mid": v(-15.98, -32.7) * mm, "end": v(-16.82, -33.14) * mm});
            skArc(sketch, "E707", {"start": v(-16.82, -33.14) * mm, "mid": v(-18.1, -34.94) * mm, "end": v(-18.93, -36.98) * mm});
            skArc(sketch, "E708", {"start": v(-18.93, -36.98) * mm, "mid": v(-18.95, -37.24) * mm, "end": v(-18.9, -37.5) * mm});
            skLineSegment(sketch, "E709", {"start": v(-18.9, -37.5) * mm, "end": v(-17.92, -40.55) * mm});
            skLineSegment(sketch, "E710", {"start": v(-17.92, -40.55) * mm, "end": v(-16.27, -40.55) * mm});
            skArc(sketch, "E711", {"start": v(-16.27, -40.55) * mm, "mid": v(-16.06, -40.64) * mm, "end": v(-15.97, -40.85) * mm});
            skLineSegment(sketch, "E712", {"start": v(-15.97, -40.85) * mm, "end": v(-15.97, -42.55) * mm});
            skLineSegment(sketch, "E713", {"start": v(-15.97, -42.55) * mm, "end": v(-16.77, -43.05) * mm});
            skLineSegment(sketch, "E714", {"start": v(-16.77, -43.05) * mm, "end": v(-26.82, -43.05) * mm});
            skArc(sketch, "E715", {"start": v(-26.82, -43.05) * mm, "mid": v(-27.52, -42.76) * mm, "end": v(-27.82, -42.05) * mm});
            skLineSegment(sketch, "E716", {"start": v(-27.82, -42.05) * mm, "end": v(-27.82, -32) * mm});
            skLineSegment(sketch, "E717", {"start": v(-27.82, -32) * mm, "end": v(-27.32, -31.2) * mm});
            skLineSegment(sketch, "E718", {"start": v(-27.32, -31.2) * mm, "end": v(-25.62, -31.2) * mm});
            skArc(sketch, "E719", {"start": v(-25.62, -31.2) * mm, "mid": v(-25.4, -31.3) * mm, "end": v(-25.32, -31.5) * mm});
            skLineSegment(sketch, "E720", {"start": v(-25.32, -31.5) * mm, "end": v(-25.32, -33.15) * mm});
            skLineSegment(sketch, "E721", {"start": v(-25.32, -33.15) * mm, "end": v(-22.27, -34.14) * mm});
            skArc(sketch, "E722", {"start": v(-22.27, -34.14) * mm, "mid": v(-22, -34.19) * mm, "end": v(-21.75, -34.17) * mm});
            skArc(sketch, "E723", {"start": v(-21.75, -34.17) * mm, "mid": v(-19.7, -33.33) * mm, "end": v(-17.9, -32.06) * mm});
            skArc(sketch, "E724", {"start": v(-17.9, -32.06) * mm, "mid": v(-17.47, -31.21) * mm, "end": v(-17.32, -30.27) * mm});
            skLineSegment(sketch, "E725", {"start": v(-17.32, -30.27) * mm, "end": v(-17.32, -28.55) * mm});
            skLineSegment(sketch, "E726", {"start": v(-17.32, -28.55) * mm, "end": v(-16.82, -28.05) * mm});
            skLineSegment(sketch, "E727", {"start": v(-16.82, -28.05) * mm, "end": v(-17.32, -27.55) * mm});
            skLineSegment(sketch, "E728", {"start": v(-17.32, -27.55) * mm, "end": v(-17.32, -25.84) * mm});
            skArc(sketch, "E729", {"start": v(-17.32, -25.84) * mm, "mid": v(-17.47, -24.9) * mm, "end": v(-17.9, -24.05) * mm});
            skArc(sketch, "E730", {"start": v(-17.9, -24.05) * mm, "mid": v(-19.7, -22.78) * mm, "end": v(-21.75, -21.94) * mm});
            skArc(sketch, "E731", {"start": v(-21.75, -21.94) * mm, "mid": v(-22, -21.92) * mm, "end": v(-22.27, -21.97) * mm});
            skLineSegment(sketch, "E732", {"start": v(-22.27, -21.97) * mm, "end": v(-25.32, -22.95) * mm});
            skLineSegment(sketch, "E733", {"start": v(-25.32, -22.95) * mm, "end": v(-25.32, -24.6) * mm});
            skArc(sketch, "E734", {"start": v(-25.32, -24.6) * mm, "mid": v(-25.4, -24.82) * mm, "end": v(-25.62, -24.9) * mm});
            skLineSegment(sketch, "E735", {"start": v(-25.62, -24.9) * mm, "end": v(-27.32, -24.9) * mm});
            skLineSegment(sketch, "E736", {"start": v(-27.32, -24.9) * mm, "end": v(-27.82, -24.1) * mm});
            skLineSegment(sketch, "E737", {"start": v(-27.82, -24.1) * mm, "end": v(-27.82, -14.05) * mm});
            skArc(sketch, "E738", {"start": v(-27.82, -14.05) * mm, "mid": v(-27.52, -13.35) * mm, "end": v(-26.82, -13.05) * mm});
            skLineSegment(sketch, "E739", {"start": v(-26.82, -13.05) * mm, "end": v(-16.77, -13.05) * mm});
            skLineSegment(sketch, "E740", {"start": v(-16.77, -13.05) * mm, "end": v(-15.97, -13.55) * mm});
            skLineSegment(sketch, "E741", {"start": v(-15.97, -13.55) * mm, "end": v(-15.97, -15.25) * mm});
            skArc(sketch, "E742", {"start": v(-15.97, -15.25) * mm, "mid": v(-16.06, -15.47) * mm, "end": v(-16.27, -15.55) * mm});
            skLineSegment(sketch, "E743", {"start": v(-16.27, -15.55) * mm, "end": v(-17.92, -15.55) * mm});
            skLineSegment(sketch, "E744", {"start": v(-17.92, -15.55) * mm, "end": v(-18.9, -18.6) * mm});
            skArc(sketch, "E745", {"start": v(-18.9, -18.6) * mm, "mid": v(-18.95, -18.86) * mm, "end": v(-18.93, -19.13) * mm});
            skArc(sketch, "E746", {"start": v(-18.93, -19.13) * mm, "mid": v(-18.1, -21.16) * mm, "end": v(-16.82, -22.96) * mm});
            skArc(sketch, "E747", {"start": v(-16.82, -22.96) * mm, "mid": v(-15.98, -23.4) * mm, "end": v(-15.04, -23.55) * mm});
            skLineSegment(sketch, "E748", {"start": v(-15.04, -23.55) * mm, "end": v(-13.32, -23.55) * mm});
            skLineSegment(sketch, "E749", {"start": v(-13.32, -23.55) * mm, "end": v(-12.82, -24.05) * mm});
            skLineSegment(sketch, "E750", {"start": v(-12.82, -24.05) * mm, "end": v(-12.32, -23.55) * mm});
            skLineSegment(sketch, "E751", {"start": v(-12.32, -23.55) * mm, "end": v(-10.6, -23.55) * mm});
            skArc(sketch, "E752", {"start": v(-10.6, -23.55) * mm, "mid": v(-9.66, -23.4) * mm, "end": v(-8.81, -22.96) * mm});
            skArc(sketch, "E753", {"start": v(-8.81, -22.96) * mm, "mid": v(-7.54, -21.16) * mm, "end": v(-6.7, -19.13) * mm});
            skArc(sketch, "E754", {"start": v(-6.7, -19.13) * mm, "mid": v(-6.68, -18.86) * mm, "end": v(-6.73, -18.6) * mm});
            skLineSegment(sketch, "E755", {"start": v(-6.73, -18.6) * mm, "end": v(-7.72, -15.55) * mm});
            skLineSegment(sketch, "E756", {"start": v(-7.72, -15.55) * mm, "end": v(-9.37, -15.55) * mm});
            skArc(sketch, "E757", {"start": v(-9.37, -15.55) * mm, "mid": v(-9.58, -15.47) * mm, "end": v(-9.67, -15.25) * mm});
            skLineSegment(sketch, "E758", {"start": v(-9.67, -15.25) * mm, "end": v(-9.67, -13.55) * mm});
            skLineSegment(sketch, "E759", {"start": v(-9.67, -13.55) * mm, "end": v(-8.87, -13.05) * mm});
            skLineSegment(sketch, "E760", {"start": v(-8.87, -13.05) * mm, "end": v(1.18, -13.05) * mm});
            skArc(sketch, "E761", {"start": v(1.18, -13.05) * mm, "mid": v(1.89, -13.35) * mm, "end": v(2.18, -14.05) * mm});
            skLineSegment(sketch, "E762", {"start": v(2.18, -14.05) * mm, "end": v(2.18, -24.1) * mm});
            skLineSegment(sketch, "E763", {"start": v(2.18, -24.1) * mm, "end": v(1.68, -24.9) * mm});
            skLineSegment(sketch, "E764", {"start": v(1.68, -24.9) * mm, "end": v(-0.02, -24.9) * mm});
            skArc(sketch, "E765", {"start": v(-0.02, -24.9) * mm, "mid": v(-0.23, -24.82) * mm, "end": v(-0.32, -24.6) * mm});
            skLineSegment(sketch, "E766", {"start": v(-0.32, -24.6) * mm, "end": v(-0.32, -22.95) * mm});
            skLineSegment(sketch, "E767", {"start": v(-0.32, -22.95) * mm, "end": v(-3.37, -21.97) * mm});
            skArc(sketch, "E768", {"start": v(-3.37, -21.97) * mm, "mid": v(-3.63, -21.92) * mm, "end": v(-3.9, -21.94) * mm});
            skArc(sketch, "E769", {"start": v(-3.9, -21.94) * mm, "mid": v(-5.93, -22.78) * mm, "end": v(-7.73, -24.05) * mm});
            skArc(sketch, "E770", {"start": v(-7.73, -24.05) * mm, "mid": v(-8.17, -24.9) * mm, "end": v(-8.32, -25.84) * mm});
            skLineSegment(sketch, "E771", {"start": v(-8.32, -25.84) * mm, "end": v(-8.32, -27.55) * mm});
            skLineSegment(sketch, "E772", {"start": v(-8.32, -27.55) * mm, "end": v(-8.82, -28.05) * mm});
            skLineSegment(sketch, "E773", {"start": v(-8.82, -28.05) * mm, "end": v(-8.32, -28.55) * mm});
            skLineSegment(sketch, "E774", {"start": v(-8.32, -28.55) * mm, "end": v(-8.32, -30.27) * mm});
            skArc(sketch, "E775", {"start": v(-8.32, -30.27) * mm, "mid": v(-8.17, -31.21) * mm, "end": v(-7.73, -32.06) * mm});
            skArc(sketch, "E776", {"start": v(-7.73, -32.06) * mm, "mid": v(-5.93, -33.33) * mm, "end": v(-3.9, -34.17) * mm});
            skArc(sketch, "E777", {"start": v(-3.9, -34.17) * mm, "mid": v(-3.63, -34.19) * mm, "end": v(-3.37, -34.14) * mm});
            skLineSegment(sketch, "E778", {"start": v(-3.37, -34.14) * mm, "end": v(-0.32, -33.15) * mm});
            skLineSegment(sketch, "E779", {"start": v(-0.32, -33.15) * mm, "end": v(-0.32, -31.5) * mm});
            skArc(sketch, "E780", {"start": v(-0.32, -31.5) * mm, "mid": v(-0.23, -31.3) * mm, "end": v(-0.02, -31.2) * mm});
            skLineSegment(sketch, "E781", {"start": v(-0.02, -31.2) * mm, "end": v(1.68, -31.2) * mm});
            skLineSegment(sketch, "E782", {"start": v(1.68, -31.2) * mm, "end": v(2.18, -32) * mm});
            skLineSegment(sketch, "E783", {"start": v(2.18, -32) * mm, "end": v(2.18, -42.05) * mm});
            skArc(sketch, "E784", {"start": v(2.18, -42.05) * mm, "mid": v(1.89, -42.76) * mm, "end": v(1.18, -43.05) * mm});
            skLineSegment(sketch, "E785", {"start": v(1.18, -43.05) * mm, "end": v(-8.87, -43.05) * mm});
            skSolve(sketch);
        }
        {
            var Q0;
            {var subQ1=sQuery(id+"F0.wireOp",EDGE,"E636");Q0=makeQuery(id+"F0.imprint","IMPRINT",FACE,{"disambiguationData":[TD([[makeQuery(id+"F0.imprint","IMPRINT",EDGE,{"derivedFrom":subQ1}),-1.0]])]});}
            var Q1;
            Q1=makeQuery(id+"F0.imprint","IMPRINT",FACE,{"disambiguationData":[TD([[makeQuery(id+"F0.imprint","IMPRINT",EDGE,{"derivedFrom":sQuery(id+"F0.wireOp",EDGE,"E526")}),-1.0]])]});
            var Q2;
            Q2=makeQuery(id+"F0.imprint","IMPRINT",FACE,{"disambiguationData":[TD([[makeQuery(id+"F0.imprint","IMPRINT",EDGE,{"derivedFrom":sQuery(id+"F0.wireOp",EDGE,"E560")}),1.0]])]});
            var Q3;
            Q3=makeQuery(id+"F0.imprint","IMPRINT",FACE,{"disambiguationData":[TD([[makeQuery(id+"F0.imprint","IMPRINT",EDGE,{"derivedFrom":sQuery(id+"F0.wireOp",EDGE,"E592")}),-1.0]])]});
            extrude(context, id + "F1", {"entities" : qUnion([Q0, Q1, Q2, Q3]), "depth" : 240 * mm, "offsetDistance" : 25 * mm});
        }
    });
